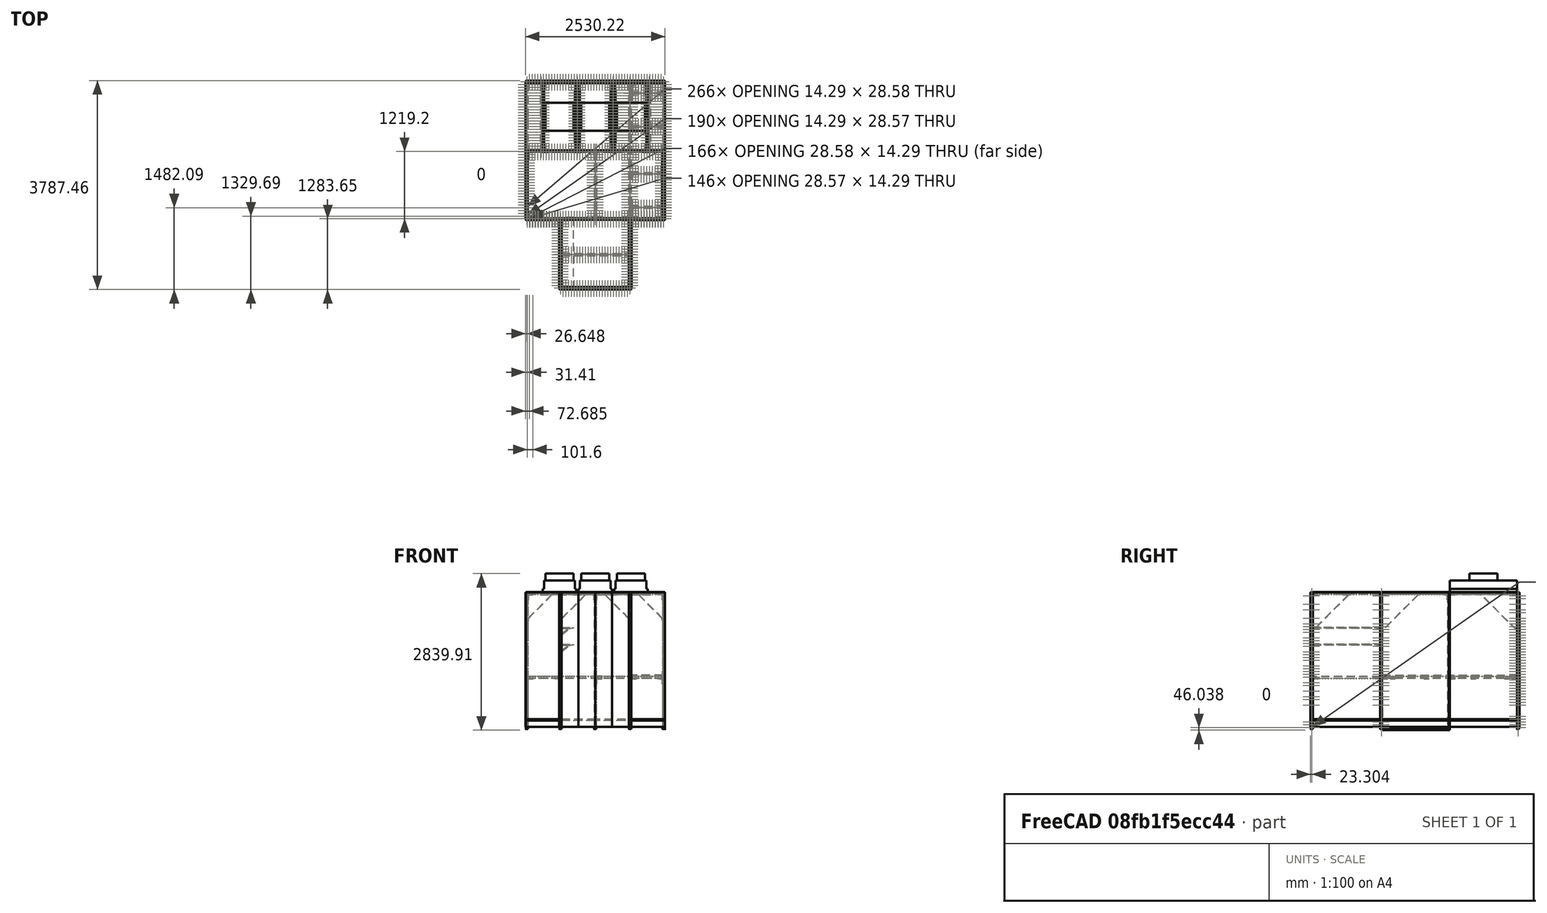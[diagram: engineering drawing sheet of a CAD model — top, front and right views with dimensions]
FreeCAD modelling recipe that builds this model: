
FCSTD DOCUMENT  (FreeCAD 0.18R16146 (Git))
Label: Clean Room
License: All rights reserved
LicenseURL: http://en.wikipedia.org/wiki/All_rights_reserved
objects: Part::Feature×99, Sketcher::SketchObject×67, PartDesign::Pad×57, PartDesign::Body×45, PartDesign::Fillet×12, PartDesign::Pocket×10, Mesh::Feature×3
note: 357 computed .brp shape members not serialized (recipe doc carries the construction recipe); baked Part::Feature solids carry a one-line shape summary decoded from their .brp

FEATURE [Part::Feature] Part__Feature  label="8ft_Strut_Channel_3310T184_001"
  Placement = pos=(-20.6375,5.55e-13,2459.29) rot=(-0.57735,-0.57735,0.57735;4.18879rad)
  shape: bbox 41.28 x 2438 x 41.28 mm, 272 faces (baked)
FEATURE [Part::Feature] Part__Feature001  label="8ft_Strut_Channel_3310T184_002"
  Placement = pos=(-2479.68,-20.6375,2459.29) rot=(-0.707107,0,0.707107;3.14159rad)
  shape: bbox 2438 x 41.28 x 41.28 mm, 272 faces (baked)
FEATURE [Part::Feature] Part__Feature002  label="8ft_Strut_Channel_3310T184_003"
  Placement = pos=(-2479.68,2459.04,2459.29) rot=(-0.707107,0,0.707107;3.14159rad)
  shape: bbox 2438 x 41.28 x 41.28 mm, 272 faces (baked)
FEATURE [Part::Feature] Part__Feature003  label="8ft_Strut_Channel_3310T184_004"
  Placement = pos=(-2500.31,5.6e-13,2459.29) rot=(-0.57735,-0.57735,0.57735;4.18879rad)
  shape: bbox 41.28 x 2438 x 41.28 mm, 272 faces (baked)
FEATURE [Part::Feature] Part__Feature004  label="8ft_Strut_Channel_3310T184_005"
  Placement = pos=(-20.6375,3e-15,20.6375) rot=(0.707107,0.707107,0;3.14159rad)
  shape: bbox 41.28 x 41.28 x 2438 mm, 272 faces (baked)
FEATURE [Part::Feature] Part__Feature005  label="8ft_Strut_Channel_3310T184_006"
  Placement = pos=(-2500.31,1.4e-14,20.6375) rot=(0.707107,0.707107,0;3.14159rad)
  shape: bbox 41.28 x 41.28 x 2438 mm, 272 faces (baked)
FEATURE [Part::Feature] Part__Feature006  label="8ft_Strut_Channel_3310T184_007"
  Placement = pos=(-2479.68,2459.04,20.6375) rot=(1,0,0;3.14159rad)
  shape: bbox 41.28 x 41.28 x 2438 mm, 272 faces (baked)
FEATURE [Part::Feature] Part__Feature007  label="8ft_Strut_Channel_3310T184_008"
  Placement = pos=(-41.021,2459.04,20.6375) rot=(0,-1,0;3.14159rad)
  shape: bbox 41.28 x 41.28 x 2438 mm, 272 faces (baked)
FEATURE [Part::Feature] Part__Feature008  label="8ft_Strut_Channel_3310T184_009"
  Placement = pos=(-650.621,-20.6375,20.6375) rot=(0,-1,0;3.14159rad)
  shape: bbox 41.28 x 41.28 x 2438 mm, 272 faces (baked)
FEATURE [Part::Feature] Part__Feature009  label="8ft_Strut_Channel_3310T184_010"
  Placement = pos=(-1911.1,-20.6375,20.6375) rot=(0,1,0;3.14159rad)
  shape: bbox 41.28 x 41.28 x 2438 mm, 272 faces (baked)
FEATURE [Part::Feature] Part__Feature010  label="8ft_Strut_Channel_3310T184_011"
  Placement = pos=(-1911.22,-1280.99,20.6375) rot=(0,1,0;3.14159rad)
  shape: bbox 41.28 x 41.28 x 2438 mm, 272 faces (baked)
FEATURE [Part::Feature] Part__Feature011  label="8ft_Strut_Channel_3310T184_012"
  Placement = pos=(-609.727,-1280.99,20.6375) rot=(1,0,0;3.14159rad)
  shape: bbox 41.28 x 41.28 x 2438 mm, 272 faces (baked)
FEATURE [Part::Feature] Part__Feature012  label="4ft_Strut_Channel_3310T181_001"
  Placement = pos=(-630.238,-1260.47,2459.29) rot=(-0.57735,-0.57735,0.57735;4.18879rad)
  shape: bbox 41.28 x 1219 x 41.28 mm, 152 faces (baked)
FEATURE [Part::Feature] Part__Feature013  label="4ft_Strut_Channel_3310T181_002"
  Placement = pos=(-650.875,-1281.11,2459.29) rot=(0,-1,0;4.71239rad)
  shape: bbox 1219 x 41.28 x 41.28 mm, 152 faces (baked)
FEATURE [Part::Feature] Part__Feature014  label="4ft_Strut_Channel_3310T181_003"
  Placement = pos=(-1890.71,-1260.47,2459.29) rot=(-0.57735,-0.57735,0.57735;4.18879rad)
  shape: bbox 41.28 x 1219 x 41.28 mm, 152 faces (baked)
FEATURE [Part::Feature] Part__Feature015  label="Double_90Deg_Bracket_33125T481_001"
  Placement = pos=(-20.6375,-20.6375,2459.04) rot=(-1,0,0;1.5708rad)
  shape: bbox 136.5 x 136.5 x 98.43 mm, 37 faces (baked)
FEATURE [Part::Feature] Part__Feature016  label="Double_90Deg_Bracket_33125T481_002"
  Placement = pos=(-2500.31,-20.6375,2459.04) rot=(0.57735,-0.57735,0.57735;4.18879rad)
  shape: bbox 136.5 x 136.5 x 98.43 mm, 37 faces (baked)
FEATURE [Part::Feature] Part__Feature017  label="Double_90Deg_Bracket_33125T481_003"
  Placement = pos=(-2500.31,2459.04,2459.04) rot=(0,0.707107,-0.707107;3.14159rad)
  shape: bbox 136.5 x 136.5 x 98.43 mm, 37 faces (baked)
FEATURE [Part::Feature] Part__Feature018  label="Double_90Deg_Bracket_33125T481_004"
  Placement = pos=(-20.6375,2459.04,2459.04) rot=(0.57735,0.57735,-0.57735;4.18879rad)
  shape: bbox 136.5 x 136.5 x 98.43 mm, 37 faces (baked)
FEATURE [Part::Feature] Part__Feature019  label="Double_90Deg_Bracket_33125T481_005"
  Placement = pos=(-1890.71,-1281.11,2459.04) rot=(0.57735,-0.57735,0.57735;4.18879rad)
  shape: bbox 136.5 x 136.5 x 98.43 mm, 37 faces (baked)
FEATURE [Part::Feature] Part__Feature020  label="Double_90Deg_Bracket_33125T481_006"
  Placement = pos=(-630.238,-1281.11,2459.04) rot=(-1,0,0;1.5708rad)
  shape: bbox 136.5 x 136.5 x 98.43 mm, 37 faces (baked)
FEATURE [Part::Feature] Part__Feature021  label="Triple_90Deg_Bracket_33125T484_001"
  Placement = pos=(-630.238,-20.6375,2459.04) rot=(0,0.707107,-0.707107;3.14159rad)
  shape: bbox 231.8 x 136.5 x 98.43 mm, 57 faces, 2 solids (baked)
FEATURE [Part::Feature] Part__Feature022  label="Triple_90Deg_Bracket_33125T484_002"
  Placement = pos=(-1890.71,-20.6375,2459.04) rot=(0,0.707107,-0.707107;3.14159rad)
  shape: bbox 231.8 x 136.5 x 98.43 mm, 57 faces, 2 solids (baked)
FEATURE [Part::Feature] Part__Feature023  label="8ft_Strut_Channel_3310T184_013"
  Placement = pos=(-2479.68,2459.04,976.312) rot=(0,-1,0;1.5708rad)
  shape: bbox 2438 x 41.28 x 41.28 mm, 272 faces (baked)
FEATURE [Part::Feature] Part__Feature024  label="8ft_Strut_Channel_3310T184_014"
  Placement = pos=(-2500.31,8.85e-13,976.312) rot=(0.57735,-0.57735,0.57735;2.0944rad)
  shape: bbox 41.28 x 2438 x 41.28 mm, 272 faces (baked)
FEATURE [Part::Feature] Part__Feature025  label="8ft_Strut_Channel_3310T184_015"
  Placement = pos=(-20.6375,2.17e-13,976.312) rot=(0.57735,-0.57735,0.57735;2.0944rad)
  shape: bbox 41.28 x 2438 x 41.28 mm, 272 faces (baked)
FEATURE [Part::Feature] Part__Feature026  label="8ft_Strut_Channel_3310T184_016"
  Placement = pos=(-630.238,2.18e-13,976.312) rot=(0.57735,-0.57735,0.57735;2.0944rad)
  shape: bbox 41.28 x 2438 x 41.28 mm, 272 faces (baked)
FEATURE [Part::Feature] Part__Feature027  label="Double_90Deg_Bracket_33125T481_007"
  Placement = pos=(-20.6375,2459.04,935.037) rot=(0.57735,0.57735,-0.57735;4.18879rad)
  shape: bbox 136.5 x 136.5 x 98.43 mm, 37 faces (baked)
FEATURE [Part::Feature] Part__Feature028  label="Double_90Deg_Bracket_33125T481_008"
  Placement = pos=(-2500.31,2459.04,935.037) rot=(0,0.707107,-0.707107;3.14159rad)
  shape: bbox 136.5 x 136.5 x 98.43 mm, 37 faces (baked)
FEATURE [Part::Feature] Part__Feature029  label="4ft_Strut_Channel_3310T181_004"
  Placement = pos=(-1890.71,-1260.47,935.291) rot=(0.57735,0.57735,-0.57735;2.0944rad)
  shape: bbox 41.28 x 1219 x 41.28 mm, 152 faces (baked)
FEATURE [Part::Feature] Part__Feature030  label="4ft_Strut_Channel_3310T181_005"
  Placement = pos=(-630.237,-1260.47,935.291) rot=(0.57735,0.57735,-0.57735;2.0944rad)
  shape: bbox 41.28 x 1219 x 41.28 mm, 152 faces (baked)
FEATURE [Part::Feature] Part__Feature031  label="2ft_Strut_Channel_3310T475_001"
  Placement = pos=(-609.6,-20.6375,976.312) rot=(0,-1,0;1.5708rad)
  shape: bbox 609.6 x 41.28 x 41.28 mm, 92 faces (baked)
FEATURE [Part::Feature] Part__Feature032  label="2ft_Strut_Channel_3310T475_002"
  Placement = pos=(-2520.95,-20.6375,976.312) rot=(0,-1,0;1.5708rad)
  shape: bbox 609.6 x 41.28 x 41.28 mm, 92 faces (baked)
FEATURE [Part::Feature] Part__Feature033  label="Double_90Deg_Bracket_33125T481_009"
  Placement = pos=(-20.6375,-20.6375,935.037) rot=(-1,0,0;1.5708rad)
  shape: bbox 136.5 x 136.5 x 98.43 mm, 37 faces (baked)
FEATURE [Part::Feature] Part__Feature034  label="Double_90Deg_Bracket_33125T481_010"
  Placement = pos=(-2500.31,-20.6375,935.037) rot=(0.57735,-0.57735,0.57735;4.18879rad)
  shape: bbox 136.5 x 136.5 x 98.43 mm, 37 faces (baked)
FEATURE [Part::Feature] Part__Feature035  label="Triple_90Deg_Bracket_33125T484_003"
  Placement = pos=(-630.238,-20.6375,935.037) rot=(0.57735,-0.57735,0.57735;4.18879rad)
  shape: bbox 136.5 x 231.8 x 98.43 mm, 57 faces, 2 solids (baked)
FEATURE [Part::Feature] Part__Feature036  label="Double_90Deg_Bracket_33125T481_011"
  Placement = pos=(-1890.71,-20.6375,935.037) rot=(0.57735,0.57735,-0.57735;4.18879rad)
  shape: bbox 136.5 x 136.5 x 98.43 mm, 37 faces (baked)
FEATURE [Part::Feature] Part__Feature037  label="90Deg_Bracket_33125T34_001"
  Placement = pos=(-630.238,-1260.48,935.037) rot=(0,1,0;1.5708rad)
  shape: bbox 41.28 x 104.8 x 88.9 mm, 18 faces (baked)
FEATURE [Part::Feature] Part__Feature038  label="90Deg_Bracket_33125T34_002"
  Placement = pos=(-1890.71,-1260.48,935.037) rot=(0,1,0;1.5708rad)
  shape: bbox 41.28 x 104.8 x 88.9 mm, 18 faces (baked)
FEATURE [Part::Feature] Part__Feature043  label="36in_Brace_3574T51_001"
  Placement = pos=(-20.5105,2115.06,2135.57) rot=(0.707107,0,0.707107;3.14159rad)
  shape: bbox 41.28 x 687.9 x 687.9 mm, 14 faces (baked)
FEATURE [Part::Feature] Part__Feature044  label="36in_Brace_3574T51_002"
  Placement = pos=(-2499.93,2115.06,2135.57) rot=(0.707107,0,0.707107;3.14159rad)
  shape: bbox 41.28 x 687.9 x 687.9 mm, 14 faces (baked)
FEATURE [Part::Feature] Part__Feature045  label="36in_Brace_3574T51_003"
  Placement = pos=(-2499.93,323.338,2135.57) rot=(-0.57735,0.57735,-0.57735;2.0944rad)
  shape: bbox 41.28 x 687.9 x 687.9 mm, 14 faces (baked)
FEATURE [Part::Feature] Part__Feature046  label="36in_Brace_3574T51_004"
  Placement = pos=(-20.5105,323.338,2135.57) rot=(-0.57735,0.57735,-0.57735;2.0944rad)
  shape: bbox 41.28 x 687.9 x 687.9 mm, 14 faces (baked)
FEATURE [Part::Feature] Part__Feature047  label="2ft_Strut_Channel_3310T475_003"
  Placement = pos=(-609.6,792.163,976.312) rot=(0,-1,0;1.5708rad)
  shape: bbox 609.6 x 41.28 x 41.28 mm, 92 faces (baked)
FEATURE [Part::Feature] Part__Feature048  label="2ft_Strut_Channel_3310T475_004"
  Placement = pos=(-609.6,1645.98,976.312) rot=(0,-1,0;1.5708rad)
  shape: bbox 609.6 x 41.28 x 41.28 mm, 92 faces (baked)
FEATURE [Part::Feature] Part__Feature049  label="Small_Tee_Bracket_33125T466_001"
  Placement = pos=(-92.2973,792.289,931.866) rot=(0,0,1;1.5708rad)
  shape: bbox 88.9 x 88.9 x 6.35 mm, 14 faces (baked)
FEATURE [Part::Feature] Part__Feature050  label="Small_Tee_Bracket_33125T466_002"
  Placement = pos=(-92.2972,1646.11,931.866) rot=(0,0,1;1.5708rad)
  shape: bbox 88.9 x 88.9 x 6.35 mm, 14 faces (baked)
FEATURE [Part::Feature] Part__Feature051  label="Small_Tee_Bracket_33125T466_003"
  Placement = pos=(-558.324,1646.11,931.866) rot=(0,0,-1;1.5708rad)
  shape: bbox 88.9 x 88.9 x 6.35 mm, 14 faces (baked)
FEATURE [Part::Feature] Part__Feature052  label="Small_Tee_Bracket_33125T466_004"
  Placement = pos=(-558.324,792.29,931.866) rot=(0,0,-1;1.5708rad)
  shape: bbox 88.9 x 88.9 x 6.35 mm, 14 faces (baked)
FEATURE [Part::Feature] Part__Feature053  label="5ft_Strut_Channel_3310T39_001"
  Placement = pos=(-20.5105,1219.2,934.91) rot=(0.707107,0.707107,0;3.14159rad)
  shape: bbox 41.28 x 41.28 x 1524 mm, 182 faces (baked)
FEATURE [Part::Feature] Part__Feature054  label="5ft_Strut_Channel_3310T39_002"
  Placement = pos=(-2499.93,1219.2,934.91) rot=(0.707107,0.707107,0;3.14159rad)
  shape: bbox 41.28 x 41.28 x 1524 mm, 182 faces (baked)
FEATURE [Part::Feature] Part__Feature055  label="5ft_Strut_Channel_3310T39_003"
  Placement = pos=(-1239.71,2458.91,934.91) rot=(1,0,0;3.14159rad)
  shape: bbox 41.28 x 41.28 x 1524 mm, 182 faces (baked)
FEATURE [Part::Feature] Part__Feature056  label="3ft_Strut_Channel_3310T54_001"
  Placement = pos=(-20.5105,1219.2,20.5105) rot=(0.707107,0.707107,0;3.14159rad)
  shape: bbox 41.28 x 41.28 x 914.4 mm, 122 faces (baked)
FEATURE [Part::Feature] Part__Feature057  label="3ft_Strut_Channel_3310T54_002"
  Placement = pos=(-2499.93,1219.2,20.5105) rot=(0.707107,0.707107,0;3.14159rad)
  shape: bbox 41.28 x 41.28 x 914.4 mm, 122 faces (baked)
FEATURE [Part::Feature] Part__Feature058  label="3ft_Strut_Channel_3310T54_003"
  Placement = pos=(-1239.71,2458.91,20.5105) rot=(1,0,0;3.14159rad)
  shape: bbox 41.28 x 41.28 x 914.4 mm, 122 faces (baked)
FEATURE [Part::Feature] Part__Feature059  label="Wraparound_Wing_Bracket_33125T491_001"
  Placement = pos=(-20.5105,1219.41,955.982) rot=(0,-1,0;1.5708rad)
  shape: bbox 47.63 x 98.43 x 232.6 mm, 44 faces (baked)
FEATURE [Part::Feature] Part__Feature061  label="Wraparound_Wing_Bracket_33125T491_002"
  Placement = pos=(-2499.93,1219.41,955.982) rot=(0,1,0;1.5708rad)
  shape: bbox 47.63 x 98.43 x 232.6 mm, 44 faces (baked)
FEATURE [Part::Feature] Part__Feature063  label="Wraparound_Wing_Bracket_33125T491_003"
  Placement = pos=(-1260.22,2459.12,2458.38) rot=(0,0.707107,-0.707107;3.14159rad)
  shape: bbox 232.6 x 47.63 x 98.43 mm, 44 faces (baked)
FEATURE [Part::Feature] Part__Feature064  label="Wraparound_Wing_Bracket_33125T491_004"
  Placement = pos=(-1239.71,2459.12,955.982) rot=(0.57735,0.57735,-0.57735;2.0944rad)
  shape: bbox 98.43 x 47.63 x 232.6 mm, 44 faces (baked)
FEATURE [Part::Feature] Part__Feature065  label="24in_Corner_Brace_3574T41_001"
  Placement = pos=(-866.569,-20.5105,2242.69) rot=(-1,0,0;1.5708rad)
  shape: bbox 472.3 x 41.28 x 472.3 mm, 14 faces (baked)
FEATURE [Part::Feature] Part__Feature066  label="24in_Corner_Brace_3574T41_002"
  Placement = pos=(-866.569,-1280.73,2242.69) rot=(-1,0,0;1.5708rad)
  shape: bbox 472.3 x 41.28 x 472.3 mm, 14 faces (baked)
FEATURE [Part::Feature] Part__Feature067  label="24in_Corner_Brace_3574T41_003"
  Placement = pos=(-1654.65,-20.5105,2242.69) rot=(0,0.707107,-0.707107;3.14159rad)
  shape: bbox 472.3 x 41.28 x 472.3 mm, 14 faces (baked)
FEATURE [Part::Feature] Part__Feature068  label="24in_Corner_Brace_3574T41_004"
  Placement = pos=(-1654.65,-1280.73,2242.69) rot=(0,0.707107,-0.707107;3.14159rad)
  shape: bbox 472.3 x 41.28 x 472.3 mm, 14 faces (baked)
FEATURE [Part::Feature] Part__Feature069  label="36in_Brace_3574T51_005"
  Placement = pos=(-630.111,-936.883,2135.57) rot=(-0.57735,0.57735,-0.57735;2.0944rad)
  shape: bbox 41.28 x 687.9 x 687.9 mm, 14 faces (baked)
FEATURE [Part::Feature] Part__Feature070  label="36in_Brace_3574T51_006"
  Placement = pos=(-1890.33,-936.883,2135.57) rot=(-0.57735,0.57735,-0.57735;2.0944rad)
  shape: bbox 41.28 x 687.9 x 687.9 mm, 14 faces (baked)
FEATURE [Part::Feature] Part__Feature071  label="24in_Corner_Brace_3574T41_005"
  Placement = pos=(-256.969,2458.91,2242.69) rot=(-1,0,0;1.5708rad)
  shape: bbox 472.3 x 41.28 x 472.3 mm, 14 faces (baked)
FEATURE [Part::Feature] Part__Feature072  label="24in_Corner_Brace_3574T41_006"
  Placement = pos=(-2264.25,2458.91,2242.69) rot=(0,0.707107,-0.707107;3.14159rad)
  shape: bbox 472.3 x 41.28 x 472.3 mm, 14 faces (baked)
FEATURE [Sketcher::SketchObject] Sketch
  MapMode = 5
  Support = -> [XY_Plane]
  sketch-geometry (4):
    g0: LineSegment StartX=0 StartY=0 StartZ=0 EndX=1219.2 EndY=0 EndZ=0
    g1: LineSegment StartX=1219.2 StartY=0 StartZ=0 EndX=1219.2 EndY=609.6 EndZ=0
    g2: LineSegment StartX=1219.2 StartY=609.6 StartZ=0 EndX=0 EndY=609.6 EndZ=0
    g3: LineSegment StartX=0 StartY=609.6 StartZ=0 EndX=0 EndY=0 EndZ=0
  constraints (11):
    c: Coincident(g0,g1)
    c: Coincident(g1,g2)
    c: Coincident(g2,g3)
    c: Coincident(g3,g0)
    c: Horizontal(g0)
    c: Horizontal(g2)
    c: Vertical(g1)
    c: Vertical(g3)
    c: Coincident(g0,g-1)
    c: DistanceX(g2,g2) = 1219.2
    c: DistanceY(g1,g1) = 609.6
FEATURE [PartDesign::Pad] Pad
  Length = 101.6
  Length2 = 100
  Profile = -> Sketch
  Type = 0
FEATURE [Sketcher::SketchObject] Sketch001
  ExternalGeometry = -> [Pad]
  MapMode = 5
  Placement = pos=(0,0,101.6) rot=(0,0,1;0rad)
  Support = -> [Pad]
  sketch-geometry (6):
    g0: LineSegment StartX=1219.2 StartY=584.2 StartZ=0 EndX=0 EndY=584.2 EndZ=0
    g1: LineSegment StartX=0 StartY=584.2 StartZ=0 EndX=0 EndY=25.4 EndZ=0
    g2: LineSegment StartX=0 StartY=25.4 StartZ=0 EndX=1219.2 EndY=25.4 EndZ=0
    g3: LineSegment StartX=1219.2 StartY=25.4 StartZ=0 EndX=1219.2 EndY=584.2 EndZ=0
    g4: LineSegment [constr] StartX=1219.2 StartY=609.6 StartZ=0 EndX=1219.2 EndY=584.2 EndZ=0
    g5: LineSegment [constr] StartX=1219.2 StartY=25.4 StartZ=0 EndX=1219.2 EndY=0 EndZ=0
  constraints (16):
    c: Coincident(g0,g1)
    c: Coincident(g1,g2)
    c: Coincident(g2,g3)
    c: Coincident(g3,g0)
    c: Horizontal(g0)
    c: Horizontal(g2)
    c: Vertical(g1)
    c: Vertical(g3)
    c: PointOnObject(g0,g-3)
    c: PointOnObject(g1,g-2)
    c: Coincident(g4,g-3)
    c: Coincident(g4,g0)
    c: Coincident(g5,g2)
    c: Coincident(g5,g-3)
    c: Equal(g5,g4)
    c: DistanceY(g4,g4) = 25.4
FEATURE [PartDesign::Pad] Pad001
  BaseFeature = -> Pad
  Length = 152.4
  Length2 = 100
  Profile = -> Sketch001
  Type = 0
FEATURE [Sketcher::SketchObject] Sketch002
  ExternalGeometry = -> [Pad001]
  MapMode = 5
  Placement = pos=(0,0,254) rot=(0,0,1;0rad)
  Support = -> [Pad001]
  sketch-geometry (8):
    g0: LineSegment StartX=355.6 StartY=558.8 StartZ=0 EndX=863.6 EndY=558.8 EndZ=0
    g1: LineSegment StartX=863.6 StartY=558.8 StartZ=0 EndX=863.6 EndY=50.8 EndZ=0
    g2: LineSegment StartX=863.6 StartY=50.8 StartZ=0 EndX=355.6 EndY=50.8 EndZ=0
    g3: LineSegment StartX=355.6 StartY=50.8 StartZ=0 EndX=355.6 EndY=558.8 EndZ=0
    g4: LineSegment [constr] StartX=863.6 StartY=558.8 StartZ=0 EndX=863.6 EndY=584.2 EndZ=0
    g5: LineSegment [constr] StartX=863.6 StartY=50.8 StartZ=0 EndX=863.6 EndY=25.4 EndZ=0
    g6: LineSegment [constr] StartX=355.6 StartY=558.8 StartZ=0 EndX=0 EndY=558.8 EndZ=0
    g7: LineSegment [constr] StartX=863.6 StartY=558.8 StartZ=0 EndX=1219.2 EndY=558.8 EndZ=0
  constraints (24):
    c: Coincident(g0,g1)
    c: Coincident(g1,g2)
    c: Coincident(g2,g3)
    c: Coincident(g3,g0)
    c: Horizontal(g0)
    c: Horizontal(g2)
    c: Vertical(g1)
    c: Vertical(g3)
    c: Coincident(g4,g0)
    c: PointOnObject(g4,g-4)
    c: Vertical(g4)
    c: Coincident(g5,g1)
    c: PointOnObject(g5,g-5)
    c: Vertical(g5)
    c: Coincident(g6,g0)
    c: PointOnObject(g6,g-2)
    c: Horizontal(g6)
    c: Coincident(g7,g0)
    c: PointOnObject(g7,g-3)
    c: Horizontal(g7)
    c: Equal(g7,g6)
    c: Equal(g4,g5)
    c: DistanceY(g4,g4) = 25.4
    c: Equal(g0,g3)
FEATURE [PartDesign::Pad] Pad002
  BaseFeature = -> Pad001
  Length = 127
  Length2 = 100
  Profile = -> Sketch002
  Type = 0
FEATURE [PartDesign::Body] Body  label="Fan_Filter_Unit_001"
  Group = -> [Sketch,Pad,Sketch001,Pad001,Sketch002,Pad002]
  Origin = -> Origin
  Placement = pos=(-307.657,1219.2,2458.91) rot=(0,0,1;1.5708rad)
  Tip = -> Pad002
FEATURE [Sketcher::SketchObject] Sketch003
  MapMode = 5
  Support = -> [XY_Plane001]
  sketch-geometry (4):
    g0: LineSegment StartX=0 StartY=0 StartZ=0 EndX=1219.2 EndY=0 EndZ=0
    g1: LineSegment StartX=1219.2 StartY=0 StartZ=0 EndX=1219.2 EndY=609.6 EndZ=0
    g2: LineSegment StartX=1219.2 StartY=609.6 StartZ=0 EndX=0 EndY=609.6 EndZ=0
    g3: LineSegment StartX=0 StartY=609.6 StartZ=0 EndX=0 EndY=0 EndZ=0
  constraints (11):
    c: Coincident(g0,g1)
    c: Coincident(g1,g2)
    c: Coincident(g2,g3)
    c: Coincident(g3,g0)
    c: Horizontal(g0)
    c: Horizontal(g2)
    c: Vertical(g1)
    c: Vertical(g3)
    c: Coincident(g0,g-1)
    c: DistanceX(g2,g2) = 1219.2
    c: DistanceY(g1,g1) = 609.6
FEATURE [PartDesign::Pad] Pad004
  Length = 101.6
  Length2 = 100
  Profile = -> Sketch003
  Type = 0
FEATURE [Sketcher::SketchObject] Sketch005
  ExternalGeometry = -> [Pad004]
  MapMode = 5
  Placement = pos=(0,0,101.6) rot=(0,0,1;0rad)
  Support = -> [Pad004]
  sketch-geometry (6):
    g0: LineSegment StartX=1219.2 StartY=584.2 StartZ=0 EndX=0 EndY=584.2 EndZ=0
    g1: LineSegment StartX=0 StartY=584.2 StartZ=0 EndX=0 EndY=25.4 EndZ=0
    g2: LineSegment StartX=0 StartY=25.4 StartZ=0 EndX=1219.2 EndY=25.4 EndZ=0
    g3: LineSegment StartX=1219.2 StartY=25.4 StartZ=0 EndX=1219.2 EndY=584.2 EndZ=0
    g4: LineSegment [constr] StartX=1219.2 StartY=609.6 StartZ=0 EndX=1219.2 EndY=584.2 EndZ=0
    g5: LineSegment [constr] StartX=1219.2 StartY=25.4 StartZ=0 EndX=1219.2 EndY=0 EndZ=0
  constraints (16):
    c: Coincident(g0,g1)
    c: Coincident(g1,g2)
    c: Coincident(g2,g3)
    c: Coincident(g3,g0)
    c: Horizontal(g0)
    c: Horizontal(g2)
    c: Vertical(g1)
    c: Vertical(g3)
    c: PointOnObject(g0,g-3)
    c: PointOnObject(g1,g-2)
    c: Coincident(g4,g-3)
    c: Coincident(g4,g0)
    c: Coincident(g5,g2)
    c: Coincident(g5,g-3)
    c: Equal(g5,g4)
    c: DistanceY(g4,g4) = 25.4
FEATURE [PartDesign::Pad] Pad005
  BaseFeature = -> Pad004
  Length = 152.4
  Length2 = 100
  Profile = -> Sketch005
  Type = 0
FEATURE [Sketcher::SketchObject] Sketch004
  ExternalGeometry = -> [Pad005]
  MapMode = 5
  Placement = pos=(0,0,254) rot=(0,0,1;0rad)
  Support = -> [Pad005]
  sketch-geometry (8):
    g0: LineSegment StartX=355.6 StartY=558.8 StartZ=0 EndX=863.6 EndY=558.8 EndZ=0
    g1: LineSegment StartX=863.6 StartY=558.8 StartZ=0 EndX=863.6 EndY=50.8 EndZ=0
    g2: LineSegment StartX=863.6 StartY=50.8 StartZ=0 EndX=355.6 EndY=50.8 EndZ=0
    g3: LineSegment StartX=355.6 StartY=50.8 StartZ=0 EndX=355.6 EndY=558.8 EndZ=0
    g4: LineSegment [constr] StartX=863.6 StartY=558.8 StartZ=0 EndX=863.6 EndY=584.2 EndZ=0
    g5: LineSegment [constr] StartX=863.6 StartY=50.8 StartZ=0 EndX=863.6 EndY=25.4 EndZ=0
    g6: LineSegment [constr] StartX=355.6 StartY=558.8 StartZ=0 EndX=0 EndY=558.8 EndZ=0
    g7: LineSegment [constr] StartX=863.6 StartY=558.8 StartZ=0 EndX=1219.2 EndY=558.8 EndZ=0
  constraints (24):
    c: Coincident(g0,g1)
    c: Coincident(g1,g2)
    c: Coincident(g2,g3)
    c: Coincident(g3,g0)
    c: Horizontal(g0)
    c: Horizontal(g2)
    c: Vertical(g1)
    c: Vertical(g3)
    c: Coincident(g4,g0)
    c: PointOnObject(g4,g-4)
    c: Vertical(g4)
    c: Coincident(g5,g1)
    c: PointOnObject(g5,g-5)
    c: Vertical(g5)
    c: Coincident(g6,g0)
    c: PointOnObject(g6,g-2)
    c: Horizontal(g6)
    c: Coincident(g7,g0)
    c: PointOnObject(g7,g-3)
    c: Horizontal(g7)
    c: Equal(g7,g6)
    c: Equal(g4,g5)
    c: DistanceY(g4,g4) = 25.4
    c: Equal(g0,g3)
FEATURE [PartDesign::Pad] Pad003
  BaseFeature = -> Pad005
  Length = 127
  Length2 = 100
  Profile = -> Sketch004
  Type = 0
FEATURE [PartDesign::Body] Body001  label="Fan_Filter_Unit_002"
  Group = -> [Sketch003,Pad004,Sketch005,Pad005,Sketch004,Pad003]
  Origin = -> Origin001
  Placement = pos=(-1603.18,1219.2,2458.91) rot=(0,0,1;1.5708rad)
  Tip = -> Pad003
FEATURE [Sketcher::SketchObject] Sketch008
  MapMode = 5
  Support = -> [XY_Plane002]
  sketch-geometry (4):
    g0: LineSegment StartX=0 StartY=0 StartZ=0 EndX=1219.2 EndY=0 EndZ=0
    g1: LineSegment StartX=1219.2 StartY=0 StartZ=0 EndX=1219.2 EndY=609.6 EndZ=0
    g2: LineSegment StartX=1219.2 StartY=609.6 StartZ=0 EndX=0 EndY=609.6 EndZ=0
    g3: LineSegment StartX=0 StartY=609.6 StartZ=0 EndX=0 EndY=0 EndZ=0
  constraints (11):
    c: Coincident(g0,g1)
    c: Coincident(g1,g2)
    c: Coincident(g2,g3)
    c: Coincident(g3,g0)
    c: Horizontal(g0)
    c: Horizontal(g2)
    c: Vertical(g1)
    c: Vertical(g3)
    c: Coincident(g0,g-1)
    c: DistanceX(g2,g2) = 1219.2
    c: DistanceY(g1,g1) = 609.6
FEATURE [PartDesign::Pad] Pad008
  Length = 101.6
  Length2 = 100
  Profile = -> Sketch008
  Type = 0
FEATURE [Sketcher::SketchObject] Sketch007
  ExternalGeometry = -> [Pad008]
  MapMode = 5
  Placement = pos=(0,0,101.6) rot=(0,0,1;0rad)
  Support = -> [Pad008]
  sketch-geometry (6):
    g0: LineSegment StartX=1219.2 StartY=584.2 StartZ=0 EndX=0 EndY=584.2 EndZ=0
    g1: LineSegment StartX=0 StartY=584.2 StartZ=0 EndX=0 EndY=25.4 EndZ=0
    g2: LineSegment StartX=0 StartY=25.4 StartZ=0 EndX=1219.2 EndY=25.4 EndZ=0
    g3: LineSegment StartX=1219.2 StartY=25.4 StartZ=0 EndX=1219.2 EndY=584.2 EndZ=0
    g4: LineSegment [constr] StartX=1219.2 StartY=609.6 StartZ=0 EndX=1219.2 EndY=584.2 EndZ=0
    g5: LineSegment [constr] StartX=1219.2 StartY=25.4 StartZ=0 EndX=1219.2 EndY=0 EndZ=0
  constraints (16):
    c: Coincident(g0,g1)
    c: Coincident(g1,g2)
    c: Coincident(g2,g3)
    c: Coincident(g3,g0)
    c: Horizontal(g0)
    c: Horizontal(g2)
    c: Vertical(g1)
    c: Vertical(g3)
    c: PointOnObject(g0,g-3)
    c: PointOnObject(g1,g-2)
    c: Coincident(g4,g-3)
    c: Coincident(g4,g0)
    c: Coincident(g5,g2)
    c: Coincident(g5,g-3)
    c: Equal(g5,g4)
    c: DistanceY(g4,g4) = 25.4
FEATURE [PartDesign::Pad] Pad006
  BaseFeature = -> Pad008
  Length = 152.4
  Length2 = 100
  Profile = -> Sketch007
  Type = 0
FEATURE [Sketcher::SketchObject] Sketch006
  ExternalGeometry = -> [Pad006]
  MapMode = 5
  Placement = pos=(0,0,254) rot=(0,0,1;0rad)
  Support = -> [Pad006]
  sketch-geometry (8):
    g0: LineSegment StartX=355.6 StartY=558.8 StartZ=0 EndX=863.6 EndY=558.8 EndZ=0
    g1: LineSegment StartX=863.6 StartY=558.8 StartZ=0 EndX=863.6 EndY=50.8 EndZ=0
    g2: LineSegment StartX=863.6 StartY=50.8 StartZ=0 EndX=355.6 EndY=50.8 EndZ=0
    g3: LineSegment StartX=355.6 StartY=50.8 StartZ=0 EndX=355.6 EndY=558.8 EndZ=0
    g4: LineSegment [constr] StartX=863.6 StartY=558.8 StartZ=0 EndX=863.6 EndY=584.2 EndZ=0
    g5: LineSegment [constr] StartX=863.6 StartY=50.8 StartZ=0 EndX=863.6 EndY=25.4 EndZ=0
    g6: LineSegment [constr] StartX=355.6 StartY=558.8 StartZ=0 EndX=0 EndY=558.8 EndZ=0
    g7: LineSegment [constr] StartX=863.6 StartY=558.8 StartZ=0 EndX=1219.2 EndY=558.8 EndZ=0
  constraints (24):
    c: Coincident(g0,g1)
    c: Coincident(g1,g2)
    c: Coincident(g2,g3)
    c: Coincident(g3,g0)
    c: Horizontal(g0)
    c: Horizontal(g2)
    c: Vertical(g1)
    c: Vertical(g3)
    c: Coincident(g4,g0)
    c: PointOnObject(g4,g-4)
    c: Vertical(g4)
    c: Coincident(g5,g1)
    c: PointOnObject(g5,g-5)
    c: Vertical(g5)
    c: Coincident(g6,g0)
    c: PointOnObject(g6,g-2)
    c: Horizontal(g6)
    c: Coincident(g7,g0)
    c: PointOnObject(g7,g-3)
    c: Horizontal(g7)
    c: Equal(g7,g6)
    c: Equal(g4,g5)
    c: DistanceY(g4,g4) = 25.4
    c: Equal(g0,g3)
FEATURE [PartDesign::Pad] Pad007
  BaseFeature = -> Pad006
  Length = 127
  Length2 = 100
  Profile = -> Sketch006
  Type = 0
FEATURE [PartDesign::Body] Body002  label="Fan_Filter_Unit_003"
  Group = -> [Sketch008,Pad008,Sketch007,Pad006,Sketch006,Pad007]
  Origin = -> Origin002
  Placement = pos=(-955.421,1219.2,2458.91) rot=(0,0,1;1.5708rad)
  Tip = -> Pad007
FEATURE [Part::Feature] Part__Feature073  label="8ft_Strut_Channel_3310T184_017"
  Placement = pos=(-2479.68,1198.56,2459.29) rot=(-0.707107,0,0.707107;3.14159rad)
  shape: bbox 2438 x 41.28 x 41.28 mm, 272 faces (baked)
FEATURE [Part::Feature] Part__Feature074  label="4ft_Strut_Channel_3310T181_006"
  Placement = pos=(-281.559,1218.95,2459.29) rot=(-0.57735,-0.57735,0.57735;4.18879rad)
  shape: bbox 41.28 x 1219 x 41.28 mm, 152 faces (baked)
FEATURE [Part::Feature] Part__Feature075  label="4ft_Strut_Channel_3310T181_007"
  Placement = pos=(-935.331,1218.95,2500.31) rot=(0.57735,-0.57735,0.57735;2.0944rad)
  shape: bbox 41.28 x 1219 x 41.28 mm, 152 faces (baked)
FEATURE [Part::Feature] Part__Feature076  label="4ft_Strut_Channel_3310T181_008"
  Placement = pos=(-1586.54,1218.95,2500.31) rot=(0.57735,-0.57735,0.57735;2.0944rad)
  shape: bbox 41.28 x 1219 x 41.28 mm, 152 faces (baked)
FEATURE [Part::Feature] Part__Feature077  label="4ft_Strut_Channel_3310T181_009"
  Placement = pos=(-2237.75,1218.95,2459.29) rot=(-0.57735,-0.57735,0.57735;4.18879rad)
  shape: bbox 41.28 x 1219 x 41.28 mm, 152 faces (baked)
FEATURE [Part::Feature] Part__Feature078  label="Triple_90Deg_Bracket_33125T484_004"
  Placement = pos=(-2500.9,1199.74,2459.04) rot=(0.57735,-0.57735,0.57735;4.18879rad)
  shape: bbox 136.5 x 231.8 x 98.43 mm, 57 faces, 2 solids (baked)
FEATURE [Part::Feature] Part__Feature079  label="Triple_90Deg_Bracket_33125T484_005"
  Placement = pos=(-21.4789,1199.74,2459.04) rot=(0.57735,0.57735,-0.57735;4.18879rad)
  shape: bbox 136.5 x 231.8 x 98.43 mm, 57 faces, 2 solids (baked)
FEATURE [Part::Feature] Part__Feature080  label="Large_Elbow_33125T22_001"
  Placement = pos=(-562.116,2390.97,932.587) rot=(0,0,-1;1.5708rad)
  shape: bbox 136.5 x 136.5 x 6.35 mm, 17 faces (baked)
FEATURE [Part::Feature] Part__Feature081  label="Large_Elbow_33125T22_002"
  Placement = pos=(-349.96,2390.97,2456.59) rot=(0,0,1;3.14159rad)
  shape: bbox 136.5 x 136.5 x 6.35 mm, 17 faces (baked)
FEATURE [Part::Feature] Part__Feature082  label="Large_Elbow_33125T22_003"
  Placement = pos=(-349.96,1266.63,2456.59) rot=(0,0,1;1.5708rad)
  shape: bbox 136.5 x 136.5 x 6.35 mm, 17 faces (baked)
FEATURE [Part::Feature] Part__Feature083  label="Large_Elbow_33125T22_004"
  Placement = pos=(-2169.63,1266.63,2456.59) rot=(0,0,1;0rad)
  shape: bbox 136.5 x 136.5 x 6.35 mm, 17 faces (baked)
FEATURE [Part::Feature] Part__Feature084  label="Large_Elbow_33125T22_005"
  Placement = pos=(-2169.63,2390.86,2456.59) rot=(0,0,-1;1.5708rad)
  shape: bbox 136.5 x 136.5 x 6.35 mm, 17 faces (baked)
FEATURE [Part::Feature] Part__Feature085  label="Large_Tee_Bracket_33125T77_001"
  Placement = pos=(-935.551,2343.22,2455.71) rot=(0,0,1;3.14159rad)
  shape: bbox 136.5 x 136.5 x 6.35 mm, 18 faces (baked)
FEATURE [Part::Feature] Part__Feature086  label="Large_Tee_Bracket_33125T77_002"
  Placement = pos=(-1586.76,2343.22,2455.71) rot=(0,0,1;3.14159rad)
  shape: bbox 136.5 x 136.5 x 6.35 mm, 18 faces (baked)
FEATURE [Part::Feature] Part__Feature087  label="Large_Tee_Bracket_33125T77_003"
  Placement = pos=(-1586.76,1314.49,2455.71) rot=(0,0,1;0rad)
  shape: bbox 136.5 x 136.5 x 6.35 mm, 18 faces (baked)
FEATURE [Part::Feature] Part__Feature088  label="Large_Tee_Bracket_33125T77_004"
  Placement = pos=(-935.551,1314.49,2455.71) rot=(0,0,1;0rad)
  shape: bbox 136.5 x 136.5 x 6.35 mm, 18 faces (baked)
FEATURE [Sketcher::SketchObject] Sketch009
  MapMode = 5
  Placement = pos=(0,0,0) rot=(0.57735,0.57735,0.57735;2.0944rad)
  Support = -> [YZ_Plane003]
  sketch-geometry (4):
    g0: LineSegment StartX=0 StartY=0 StartZ=0 EndX=1219.2 EndY=0 EndZ=0
    g1: LineSegment StartX=1219.2 StartY=0 StartZ=0 EndX=1219.2 EndY=2438.4 EndZ=0
    g2: LineSegment StartX=1219.2 StartY=2438.4 StartZ=0 EndX=0 EndY=2438.4 EndZ=0
    g3: LineSegment StartX=0 StartY=2438.4 StartZ=0 EndX=0 EndY=0 EndZ=0
  constraints (11):
    c: Coincident(g0,g1)
    c: Coincident(g1,g2)
    c: Coincident(g2,g3)
    c: Coincident(g3,g0)
    c: Horizontal(g0)
    c: Horizontal(g2)
    c: Vertical(g1)
    c: Vertical(g3)
    c: Coincident(g0,g-1)
    c: DistanceX(g0,g0) = 1219.2
    c: DistanceY(g1,g1) = 2438.4
FEATURE [PartDesign::Pad] Pad009
  Length = 2.032
  Length2 = 100
  Placement = pos=(0,0,0) rot=(0.57735,0.57735,0.57735;2.0944rad)
  Profile = -> Sketch009
  Type = 0
FEATURE [PartDesign::Body] Body003  label="4ftx8ft_Acrylic_Panel_001"
  Group = -> [Sketch009,Pad009]
  Origin = -> Origin003
  Placement = pos=(0.254,-20.5105,61.6585) rot=(0,0,1;0rad)
  Tip = -> Pad009
FEATURE [Sketcher::SketchObject] Sketch010
  MapMode = 5
  Placement = pos=(0,0,0) rot=(0.57735,0.57735,0.57735;2.0944rad)
  Support = -> [YZ_Plane004]
  sketch-geometry (4):
    g0: LineSegment StartX=0 StartY=0 StartZ=0 EndX=1219.2 EndY=0 EndZ=0
    g1: LineSegment StartX=1219.2 StartY=0 StartZ=0 EndX=1219.2 EndY=2438.4 EndZ=0
    g2: LineSegment StartX=1219.2 StartY=2438.4 StartZ=0 EndX=0 EndY=2438.4 EndZ=0
    g3: LineSegment StartX=0 StartY=2438.4 StartZ=0 EndX=0 EndY=0 EndZ=0
  constraints (11):
    c: Coincident(g0,g1)
    c: Coincident(g1,g2)
    c: Coincident(g2,g3)
    c: Coincident(g3,g0)
    c: Horizontal(g0)
    c: Horizontal(g2)
    c: Vertical(g1)
    c: Vertical(g3)
    c: Coincident(g0,g-1)
    c: DistanceX(g0,g0) = 1219.2
    c: DistanceY(g1,g1) = 2438.4
FEATURE [PartDesign::Pad] Pad010
  Length = 2.032
  Length2 = 100
  Placement = pos=(0,0,0) rot=(0.57735,0.57735,0.57735;2.0944rad)
  Profile = -> Sketch010
  Type = 0
FEATURE [PartDesign::Body] Body004  label="4ftx8ft_Acrylic_Panel_002"
  Group = -> [Sketch010,Pad010]
  Origin = -> Origin004
  Placement = pos=(0.254,1219.2,61.6585) rot=(0,0,1;0rad)
  Tip = -> Pad010
FEATURE [Sketcher::SketchObject] Sketch011
  MapMode = 5
  Placement = pos=(0,0,0) rot=(0.57735,0.57735,0.57735;2.0944rad)
  Support = -> [YZ_Plane005]
  sketch-geometry (4):
    g0: LineSegment StartX=0 StartY=0 StartZ=0 EndX=1219.2 EndY=0 EndZ=0
    g1: LineSegment StartX=1219.2 StartY=0 StartZ=0 EndX=1219.2 EndY=2438.4 EndZ=0
    g2: LineSegment StartX=1219.2 StartY=2438.4 StartZ=0 EndX=0 EndY=2438.4 EndZ=0
    g3: LineSegment StartX=0 StartY=2438.4 StartZ=0 EndX=0 EndY=0 EndZ=0
  constraints (11):
    c: Coincident(g0,g1)
    c: Coincident(g1,g2)
    c: Coincident(g2,g3)
    c: Coincident(g3,g0)
    c: Horizontal(g0)
    c: Horizontal(g2)
    c: Vertical(g1)
    c: Vertical(g3)
    c: Coincident(g0,g-1)
    c: DistanceX(g0,g0) = 1219.2
    c: DistanceY(g1,g1) = 2438.4
FEATURE [PartDesign::Pad] Pad011
  Length = 2.032
  Length2 = 100
  Placement = pos=(0,0,0) rot=(0.57735,0.57735,0.57735;2.0944rad)
  Profile = -> Sketch011
  Type = 0
FEATURE [PartDesign::Body] Body005  label="4ftx8ft_Acrylic_Panel_003"
  Group = -> [Sketch011,Pad011]
  Origin = -> Origin005
  Placement = pos=(-2524.25,-20.5105,61.6585) rot=(0,0,1;0rad)
  Tip = -> Pad011
FEATURE [Sketcher::SketchObject] Sketch012
  MapMode = 5
  Placement = pos=(0,0,0) rot=(0.57735,0.57735,0.57735;2.0944rad)
  Support = -> [YZ_Plane006]
  sketch-geometry (4):
    g0: LineSegment StartX=0 StartY=0 StartZ=0 EndX=1219.2 EndY=0 EndZ=0
    g1: LineSegment StartX=1219.2 StartY=0 StartZ=0 EndX=1219.2 EndY=2438.4 EndZ=0
    g2: LineSegment StartX=1219.2 StartY=2438.4 StartZ=0 EndX=0 EndY=2438.4 EndZ=0
    g3: LineSegment StartX=0 StartY=2438.4 StartZ=0 EndX=0 EndY=0 EndZ=0
  constraints (11):
    c: Coincident(g0,g1)
    c: Coincident(g1,g2)
    c: Coincident(g2,g3)
    c: Coincident(g3,g0)
    c: Horizontal(g0)
    c: Horizontal(g2)
    c: Vertical(g1)
    c: Vertical(g3)
    c: Coincident(g0,g-1)
    c: DistanceX(g0,g0) = 1219.2
    c: DistanceY(g1,g1) = 2438.4
FEATURE [PartDesign::Pad] Pad012
  Length = 2.032
  Length2 = 100
  Placement = pos=(0,0,0) rot=(0.57735,0.57735,0.57735;2.0944rad)
  Profile = -> Sketch012
  Type = 0
FEATURE [PartDesign::Body] Body006  label="4ftx8ft_Acrylic_Panel_004"
  Group = -> [Sketch012,Pad012]
  Origin = -> Origin006
  Placement = pos=(-2524.25,1219.2,61.6585) rot=(0,0,1;0rad)
  Tip = -> Pad012
FEATURE [Sketcher::SketchObject] Sketch013
  MapMode = 5
  Placement = pos=(0,0,0) rot=(0.57735,0.57735,0.57735;2.0944rad)
  Support = -> [YZ_Plane007]
  sketch-geometry (4):
    g0: LineSegment StartX=0 StartY=0 StartZ=0 EndX=1219.2 EndY=0 EndZ=0
    g1: LineSegment StartX=1219.2 StartY=0 StartZ=0 EndX=1219.2 EndY=2438.4 EndZ=0
    g2: LineSegment StartX=1219.2 StartY=2438.4 StartZ=0 EndX=0 EndY=2438.4 EndZ=0
    g3: LineSegment StartX=0 StartY=2438.4 StartZ=0 EndX=0 EndY=0 EndZ=0
  constraints (11):
    c: Coincident(g0,g1)
    c: Coincident(g1,g2)
    c: Coincident(g2,g3)
    c: Coincident(g3,g0)
    c: Horizontal(g0)
    c: Horizontal(g2)
    c: Vertical(g1)
    c: Vertical(g3)
    c: Coincident(g0,g-1)
    c: DistanceX(g0,g0) = 1219.2
    c: DistanceY(g1,g1) = 2438.4
FEATURE [PartDesign::Pad] Pad013
  Length = 2.032
  Length2 = 100
  Placement = pos=(0,0,0) rot=(0.57735,0.57735,0.57735;2.0944rad)
  Profile = -> Sketch013
  Type = 0
FEATURE [PartDesign::Body] Body007  label="4ftx8ft_Acrylic_Panel_005"
  Group = -> [Sketch013,Pad013]
  Origin = -> Origin007
  Placement = pos=(-30.5117,2479.42,61.6585) rot=(0,0,1;1.5708rad)
  Tip = -> Pad013
FEATURE [Sketcher::SketchObject] Sketch014
  MapMode = 5
  Placement = pos=(0,0,0) rot=(0.57735,0.57735,0.57735;2.0944rad)
  Support = -> [YZ_Plane008]
  sketch-geometry (4):
    g0: LineSegment StartX=0 StartY=0 StartZ=0 EndX=1219.2 EndY=0 EndZ=0
    g1: LineSegment StartX=1219.2 StartY=0 StartZ=0 EndX=1219.2 EndY=2438.4 EndZ=0
    g2: LineSegment StartX=1219.2 StartY=2438.4 StartZ=0 EndX=0 EndY=2438.4 EndZ=0
    g3: LineSegment StartX=0 StartY=2438.4 StartZ=0 EndX=0 EndY=0 EndZ=0
  constraints (11):
    c: Coincident(g0,g1)
    c: Coincident(g1,g2)
    c: Coincident(g2,g3)
    c: Coincident(g3,g0)
    c: Horizontal(g0)
    c: Horizontal(g2)
    c: Vertical(g1)
    c: Vertical(g3)
    c: Coincident(g0,g-1)
    c: DistanceX(g0,g0) = 1219.2
    c: DistanceY(g1,g1) = 2438.4
FEATURE [PartDesign::Pad] Pad014
  Length = 2.032
  Length2 = 100
  Placement = pos=(0,0,0) rot=(0.57735,0.57735,0.57735;2.0944rad)
  Profile = -> Sketch014
  Type = 0
FEATURE [PartDesign::Body] Body008  label="4ftx8ft_Acrylic_Panel_006"
  Group = -> [Sketch014,Pad014]
  Origin = -> Origin008
  Placement = pos=(-1270.22,2479.42,61.6585) rot=(0,0,1;1.5708rad)
  Tip = -> Pad014
FEATURE [Sketcher::SketchObject] Sketch015
  MapMode = 5
  Placement = pos=(0,0,0) rot=(0.57735,0.57735,0.57735;2.0944rad)
  Support = -> [YZ_Plane009]
  sketch-geometry (4):
    g0: LineSegment StartX=0 StartY=0 StartZ=0 EndX=1219.2 EndY=0 EndZ=0
    g1: LineSegment StartX=1219.2 StartY=0 StartZ=0 EndX=1219.2 EndY=2438.4 EndZ=0
    g2: LineSegment StartX=1219.2 StartY=2438.4 StartZ=0 EndX=0 EndY=2438.4 EndZ=0
    g3: LineSegment StartX=0 StartY=2438.4 StartZ=0 EndX=0 EndY=0 EndZ=0
  constraints (11):
    c: Coincident(g0,g1)
    c: Coincident(g1,g2)
    c: Coincident(g2,g3)
    c: Coincident(g3,g0)
    c: Horizontal(g0)
    c: Horizontal(g2)
    c: Vertical(g1)
    c: Vertical(g3)
    c: Coincident(g0,g-1)
    c: DistanceX(g0,g0) = 1219.2
    c: DistanceY(g1,g1) = 2438.4
FEATURE [PartDesign::Pad] Pad015
  Length = 2.032
  Length2 = 100
  Placement = pos=(0,0,0) rot=(0.57735,0.57735,0.57735;2.0944rad)
  Profile = -> Sketch015
  Type = 0
FEATURE [PartDesign::Body] Body009  label="4ftx8ft_Acrylic_Panel_007"
  Group = -> [Sketch015,Pad015]
  Origin = -> Origin009
  Placement = pos=(-609.346,-1260.22,61.6585) rot=(0,0,1;0rad)
  Tip = -> Pad015
FEATURE [Sketcher::SketchObject] Sketch016
  MapMode = 5
  Placement = pos=(0,0,0) rot=(0.57735,0.57735,0.57735;2.0944rad)
  Support = -> [YZ_Plane010]
  sketch-geometry (4):
    g0: LineSegment StartX=0 StartY=0 StartZ=0 EndX=1219.2 EndY=0 EndZ=0
    g1: LineSegment StartX=1219.2 StartY=0 StartZ=0 EndX=1219.2 EndY=2438.4 EndZ=0
    g2: LineSegment StartX=1219.2 StartY=2438.4 StartZ=0 EndX=0 EndY=2438.4 EndZ=0
    g3: LineSegment StartX=0 StartY=2438.4 StartZ=0 EndX=0 EndY=0 EndZ=0
  constraints (11):
    c: Coincident(g0,g1)
    c: Coincident(g1,g2)
    c: Coincident(g2,g3)
    c: Coincident(g3,g0)
    c: Horizontal(g0)
    c: Horizontal(g2)
    c: Vertical(g1)
    c: Vertical(g3)
    c: Coincident(g0,g-1)
    c: DistanceX(g0,g0) = 1219.2
    c: DistanceY(g1,g1) = 2438.4
FEATURE [PartDesign::Pad] Pad016
  Length = 2.032
  Length2 = 100
  Placement = pos=(0,0,0) rot=(0.57735,0.57735,0.57735;2.0944rad)
  Profile = -> Sketch016
  Type = 0
FEATURE [PartDesign::Body] Body010  label="4ftx8ft_Acrylic_Panel_008"
  Group = -> [Sketch016,Pad016]
  Origin = -> Origin010
  Placement = pos=(-1913.64,-1260.22,61.6585) rot=(0,0,1;0rad)
  Tip = -> Pad016
FEATURE [Sketcher::SketchObject] Sketch017
  MapMode = 5
  Placement = pos=(0,0,0) rot=(0.57735,0.57735,0.57735;2.0944rad)
  Support = -> [YZ_Plane011]
  sketch-geometry (4):
    g0: LineSegment StartX=0 StartY=0 StartZ=0 EndX=1219.2 EndY=0 EndZ=0
    g1: LineSegment StartX=1219.2 StartY=0 StartZ=0 EndX=1219.2 EndY=2438.4 EndZ=0
    g2: LineSegment StartX=1219.2 StartY=2438.4 StartZ=0 EndX=0 EndY=2438.4 EndZ=0
    g3: LineSegment StartX=0 StartY=2438.4 StartZ=0 EndX=0 EndY=0 EndZ=0
  constraints (11):
    c: Coincident(g0,g1)
    c: Coincident(g1,g2)
    c: Coincident(g2,g3)
    c: Coincident(g3,g0)
    c: Horizontal(g0)
    c: Horizontal(g2)
    c: Vertical(g1)
    c: Vertical(g3)
    c: Coincident(g0,g-1)
    c: DistanceX(g0,g0) = 1219.2
    c: DistanceY(g1,g1) = 2438.4
FEATURE [PartDesign::Pad] Pad017
  Length = 2.032
  Length2 = 100
  Placement = pos=(0,0,0) rot=(0.57735,0.57735,0.57735;2.0944rad)
  Profile = -> Sketch017
  Type = 0
FEATURE [PartDesign::Body] Body011  label="4ftx8ft_Acrylic_Panel_009"
  Group = -> [Sketch017,Pad017]
  Origin = -> Origin011
  Placement = pos=(-45.8946,-20.5105,2500.82) rot=(0,-1,0;1.5708rad)
  Tip = -> Pad017
FEATURE [Sketcher::SketchObject] Sketch018
  MapMode = 5
  Placement = pos=(0,0,0) rot=(0.57735,0.57735,0.57735;2.0944rad)
  Support = -> [YZ_Plane012]
  sketch-geometry (4):
    g0: LineSegment StartX=0 StartY=0 StartZ=0 EndX=1219.2 EndY=0 EndZ=0
    g1: LineSegment StartX=1219.2 StartY=0 StartZ=0 EndX=1219.2 EndY=1219.2 EndZ=0
    g2: LineSegment StartX=1219.2 StartY=1219.2 StartZ=0 EndX=0 EndY=1219.2 EndZ=0
    g3: LineSegment StartX=0 StartY=1219.2 StartZ=0 EndX=0 EndY=0 EndZ=0
  constraints (11):
    c: Coincident(g0,g1)
    c: Coincident(g1,g2)
    c: Coincident(g2,g3)
    c: Coincident(g3,g0)
    c: Horizontal(g0)
    c: Horizontal(g2)
    c: Vertical(g1)
    c: Vertical(g3)
    c: Coincident(g0,g-1)
    c: DistanceX(g0,g0) = 1219.2
    c: DistanceY(g1,g1) = 1219.2
FEATURE [PartDesign::Pad] Pad018
  Length = 2.032
  Length2 = 100
  Placement = pos=(0,0,0) rot=(0.57735,0.57735,0.57735;2.0944rad)
  Profile = -> Sketch018
  Type = 0
FEATURE [PartDesign::Body] Body012  label="4ftx4ft_Acrylic_Panel_001"
  Group = -> [Sketch018,Pad018]
  Origin = -> Origin012
  Placement = pos=(-650.367,-1260.22,2500.82) rot=(0,-1,0;1.5708rad)
  Tip = -> Pad018
FEATURE [Sketcher::SketchObject] Sketch019
  MapMode = 5
  Placement = pos=(0,0,0) rot=(0.57735,0.57735,0.57735;2.0944rad)
  Support = -> [YZ_Plane013]
  sketch-geometry (4):
    g0: LineSegment StartX=0 StartY=0 StartZ=0 EndX=609.6 EndY=0 EndZ=0
    g1: LineSegment StartX=609.6 StartY=0 StartZ=0 EndX=609.6 EndY=2438.4 EndZ=0
    g2: LineSegment StartX=609.6 StartY=2438.4 StartZ=0 EndX=0 EndY=2438.4 EndZ=0
    g3: LineSegment StartX=0 StartY=2438.4 StartZ=0 EndX=0 EndY=0 EndZ=0
  constraints (11):
    c: Coincident(g0,g1)
    c: Coincident(g1,g2)
    c: Coincident(g2,g3)
    c: Coincident(g3,g0)
    c: Horizontal(g0)
    c: Horizontal(g2)
    c: Vertical(g1)
    c: Vertical(g3)
    c: Coincident(g0,g-1)
    c: DistanceX(g0,g0) = 609.6
    c: DistanceY(g1,g1) = 2438.4
FEATURE [PartDesign::Pad] Pad019
  Length = 2.032
  Length2 = 100
  Placement = pos=(0,0,0) rot=(0.57735,0.57735,0.57735;2.0944rad)
  Profile = -> Sketch019
  Type = 0
FEATURE [PartDesign::Body] Body013  label="2ftx8ft_Acrylic_Panel_001"
  Group = -> [Sketch019,Pad019]
  Origin = -> Origin013
  Placement = pos=(-609.346,-41.021,61.6585) rot=(0,0,-1;1.5708rad)
  Tip = -> Pad019
FEATURE [Sketcher::SketchObject] Sketch020
  MapMode = 5
  Placement = pos=(0,0,0) rot=(0.57735,0.57735,0.57735;2.0944rad)
  Support = -> [YZ_Plane014]
  sketch-geometry (4):
    g0: LineSegment StartX=0 StartY=0 StartZ=0 EndX=609.6 EndY=0 EndZ=0
    g1: LineSegment StartX=609.6 StartY=0 StartZ=0 EndX=609.6 EndY=2438.4 EndZ=0
    g2: LineSegment StartX=609.6 StartY=2438.4 StartZ=0 EndX=0 EndY=2438.4 EndZ=0
    g3: LineSegment StartX=0 StartY=2438.4 StartZ=0 EndX=0 EndY=0 EndZ=0
  constraints (11):
    c: Coincident(g0,g1)
    c: Coincident(g1,g2)
    c: Coincident(g2,g3)
    c: Coincident(g3,g0)
    c: Horizontal(g0)
    c: Horizontal(g2)
    c: Vertical(g1)
    c: Vertical(g3)
    c: Coincident(g0,g-1)
    c: DistanceX(g0,g0) = 609.6
    c: DistanceY(g1,g1) = 2438.4
FEATURE [PartDesign::Pad] Pad020
  Length = 2.032
  Length2 = 100
  Placement = pos=(0,0,0) rot=(0.57735,0.57735,0.57735;2.0944rad)
  Profile = -> Sketch020
  Type = 0
FEATURE [PartDesign::Body] Body014  label="2ftx8ft_Acrylic_Panel_002"
  Group = -> [Sketch020,Pad020]
  Origin = -> Origin014
  Placement = pos=(-2520.19,-41.021,61.6585) rot=(0,0,-1;1.5708rad)
  Tip = -> Pad020
FEATURE [Sketcher::SketchObject] Sketch021
  MapMode = 5
  Placement = pos=(0,0,0) rot=(0.57735,0.57735,0.57735;2.0944rad)
  Support = -> [YZ_Plane015]
  sketch-geometry (4):
    g0: LineSegment StartX=0 StartY=0 StartZ=0 EndX=1219.2 EndY=0 EndZ=0
    g1: LineSegment StartX=1219.2 StartY=0 StartZ=0 EndX=1219.2 EndY=304.8 EndZ=0
    g2: LineSegment StartX=1219.2 StartY=304.8 StartZ=0 EndX=0 EndY=304.8 EndZ=0
    g3: LineSegment StartX=0 StartY=304.8 StartZ=0 EndX=0 EndY=0 EndZ=0
  constraints (11):
    c: Coincident(g0,g1)
    c: Coincident(g1,g2)
    c: Coincident(g2,g3)
    c: Coincident(g3,g0)
    c: Horizontal(g0)
    c: Horizontal(g2)
    c: Vertical(g1)
    c: Vertical(g3)
    c: Coincident(g0,g-1)
    c: DistanceX(g0,g0) = 1219.2
    c: DistanceY(g1,g1) = 304.8
FEATURE [PartDesign::Pad] Pad021
  Length = 2.032
  Length2 = 100
  Placement = pos=(0,0,0) rot=(0.57735,0.57735,0.57735;2.0944rad)
  Profile = -> Sketch021
  Type = 0
FEATURE [PartDesign::Body] Body015  label="4ftx10in_Acrylic_Panel_001"
  Group = -> [Sketch021,Pad021]
  Origin = -> Origin015
  Placement = pos=(-4.87363,1219.2,2500.82) rot=(0,-1,0;1.5708rad)
  Tip = -> Pad021
FEATURE [Sketcher::SketchObject] Sketch022
  MapMode = 5
  Placement = pos=(0,0,0) rot=(0.57735,0.57735,0.57735;2.0944rad)
  Support = -> [YZ_Plane016]
  sketch-geometry (4):
    g0: LineSegment StartX=0 StartY=0 StartZ=0 EndX=1219.2 EndY=0 EndZ=0
    g1: LineSegment StartX=1219.2 StartY=0 StartZ=0 EndX=1219.2 EndY=304.8 EndZ=0
    g2: LineSegment StartX=1219.2 StartY=304.8 StartZ=0 EndX=0 EndY=304.8 EndZ=0
    g3: LineSegment StartX=0 StartY=304.8 StartZ=0 EndX=0 EndY=0 EndZ=0
  constraints (11):
    c: Coincident(g0,g1)
    c: Coincident(g1,g2)
    c: Coincident(g2,g3)
    c: Coincident(g3,g0)
    c: Horizontal(g0)
    c: Horizontal(g2)
    c: Vertical(g1)
    c: Vertical(g3)
    c: Coincident(g0,g-1)
    c: DistanceX(g0,g0) = 1219.2
    c: DistanceY(g1,g1) = 304.8
FEATURE [PartDesign::Pad] Pad022
  Length = 2.032
  Length2 = 100
  Placement = pos=(0,0,0) rot=(0.57735,0.57735,0.57735;2.0944rad)
  Profile = -> Sketch022
  Type = 0
FEATURE [PartDesign::Body] Body016  label="4ftx10in_Acrylic_Panel_002"
  Group = -> [Sketch022,Pad022]
  Origin = -> Origin016
  Placement = pos=(-2209.75,1219.2,2500.82) rot=(0,-1,0;1.5708rad)
  Tip = -> Pad022
FEATURE [Sketcher::SketchObject] Sketch023
  MapMode = 5
  Support = -> [XY_Plane017]
  sketch-geometry (4):
    g0: LineSegment StartX=0 StartY=0 StartZ=0 EndX=-609.6 EndY=0 EndZ=0
    g1: LineSegment StartX=-609.6 StartY=0 StartZ=0 EndX=-609.6 EndY=2438.4 EndZ=0
    g2: LineSegment StartX=-609.6 StartY=2438.4 StartZ=0 EndX=0 EndY=2438.4 EndZ=0
    g3: LineSegment StartX=0 StartY=2438.4 StartZ=0 EndX=0 EndY=0 EndZ=0
  constraints (11):
    c: Coincident(g0,g1)
    c: Coincident(g1,g2)
    c: Coincident(g2,g3)
    c: Coincident(g3,g0)
    c: Horizontal(g0)
    c: Horizontal(g2)
    c: Vertical(g1)
    c: Vertical(g3)
    c: Coincident(g0,g-1)
    c: DistanceX(g2,g2) = 609.6
    c: DistanceY(g1,g1) = 2438.4
FEATURE [PartDesign::Pad] Pad023
  Length = 25.4
  Length2 = 100
  Profile = -> Sketch023
  Type = 0
FEATURE [PartDesign::Body] Body017  label="Bench_Top"
  Group = -> [Sketch023,Pad023]
  Origin = -> Origin017
  Placement = pos=(-41.021,0,975.741) rot=(0,0,1;0rad)
  Tip = -> Pad023
FEATURE [Part::Feature] Part__Feature089  label="Small_Tee_Bracket_33125T466_005"
  Placement = pos=(-558.324,182.69,931.866) rot=(0,0,-1;1.5708rad)
  shape: bbox 88.9 x 88.9 x 6.35 mm, 14 faces (baked)
FEATURE [Part::Feature] Part__Feature090  label="Small_Tee_Bracket_33125T466_006"
  Placement = pos=(-92.2973,182.689,931.866) rot=(0,0,1;1.5708rad)
  shape: bbox 88.9 x 88.9 x 6.35 mm, 14 faces (baked)
FEATURE [Part::Feature] Part__Feature091  label="2ft_Strut_Channel_3310T475_005"
  Placement = pos=(-609.6,182.563,976.312) rot=(0,-1,0;1.5708rad)
  shape: bbox 609.6 x 41.28 x 41.28 mm, 92 faces (baked)
FEATURE [Part::Feature] Part__Feature092  label="Small_Tee_Bracket_33125T466_007"
  Placement = pos=(-558.324,2255.71,931.866) rot=(0,0,-1;1.5708rad)
  shape: bbox 88.9 x 88.9 x 6.35 mm, 14 faces (baked)
FEATURE [Part::Feature] Part__Feature093  label="Small_Tee_Bracket_33125T466_008"
  Placement = pos=(-92.2972,2255.71,931.866) rot=(0,0,1;1.5708rad)
  shape: bbox 88.9 x 88.9 x 6.35 mm, 14 faces (baked)
FEATURE [Part::Feature] Part__Feature094  label="2ft_Strut_Channel_3310T475_006"
  Placement = pos=(-609.6,2255.58,976.312) rot=(0,-1,0;1.5708rad)
  shape: bbox 609.6 x 41.28 x 41.28 mm, 92 faces (baked)
FEATURE [Part::Feature] Part__Feature095  label="Shelf_Bracket_8p5in_3200T53_001"
  Placement = pos=(-1756.21,-20.5105,1849.31) rot=(1,0,0;1.5708rad)
  shape: bbox 225.4 x 41.15 x 118.7 mm, 23 faces (baked)
FEATURE [Part::Feature] Part__Feature096  label="Shelf_Bracket_8p5in_3200T53_002"
  Placement = pos=(-1756.21,-1280.73,1849.31) rot=(1,0,0;1.5708rad)
  shape: bbox 225.4 x 41.15 x 118.7 mm, 23 faces (baked)
FEATURE [Part::Feature] Part__Feature097  label="Shelf_Bracket_8p5in_3200T53_003"
  Placement = pos=(-1756.21,-1280.73,1544.51) rot=(1,0,0;1.5708rad)
  shape: bbox 225.4 x 41.15 x 118.7 mm, 23 faces (baked)
FEATURE [Part::Feature] Part__Feature098  label="Shelf_Bracket_8p5in_3200T53_004"
  Placement = pos=(-1756.21,-20.5105,1544.51) rot=(1,0,0;1.5708rad)
  shape: bbox 225.4 x 41.15 x 118.7 mm, 23 faces (baked)
FEATURE [Sketcher::SketchObject] Sketch024
  MapMode = 5
  Support = -> [XY_Plane018]
  sketch-geometry (4):
    g0: LineSegment StartX=0 StartY=0 StartZ=0 EndX=215.9 EndY=0 EndZ=0
    g1: LineSegment StartX=215.9 StartY=0 StartZ=0 EndX=215.9 EndY=1303.02 EndZ=0
    g2: LineSegment StartX=215.9 StartY=1303.02 StartZ=0 EndX=0 EndY=1303.02 EndZ=0
    g3: LineSegment StartX=0 StartY=1303.02 StartZ=0 EndX=0 EndY=0 EndZ=0
  constraints (11):
    c: Coincident(g0,g1)
    c: Coincident(g1,g2)
    c: Coincident(g2,g3)
    c: Coincident(g3,g0)
    c: Horizontal(g0)
    c: Horizontal(g2)
    c: Vertical(g1)
    c: Vertical(g3)
    c: Coincident(g0,g-1)
    c: DistanceX(g0,g0) = 215.9
    c: DistanceY(g1,g1) = 1303.02
FEATURE [PartDesign::Pad] Pad024
  Length = 12.7
  Length2 = 100
  Profile = -> Sketch024
  Type = 0
FEATURE [PartDesign::Body] Body018  label="Shelf_8p5inx51p23in_001"
  Group = -> [Sketch024,Pad024]
  Origin = -> Origin018
  Placement = pos=(-1868.81,-1301.24,1849.76) rot=(0,0,1;0rad)
  Tip = -> Pad024
FEATURE [Sketcher::SketchObject] Sketch025
  MapMode = 5
  Support = -> [XY_Plane019]
  sketch-geometry (4):
    g0: LineSegment StartX=0 StartY=0 StartZ=0 EndX=215.9 EndY=0 EndZ=0
    g1: LineSegment StartX=215.9 StartY=0 StartZ=0 EndX=215.9 EndY=1303.02 EndZ=0
    g2: LineSegment StartX=215.9 StartY=1303.02 StartZ=0 EndX=0 EndY=1303.02 EndZ=0
    g3: LineSegment StartX=0 StartY=1303.02 StartZ=0 EndX=0 EndY=0 EndZ=0
  constraints (11):
    c: Coincident(g0,g1)
    c: Coincident(g1,g2)
    c: Coincident(g2,g3)
    c: Coincident(g3,g0)
    c: Horizontal(g0)
    c: Horizontal(g2)
    c: Vertical(g1)
    c: Vertical(g3)
    c: Coincident(g0,g-1)
    c: DistanceX(g0,g0) = 215.9
    c: DistanceY(g1,g1) = 1303.02
FEATURE [PartDesign::Pad] Pad025
  Length = 12.7
  Length2 = 100
  Profile = -> Sketch025
  Type = 0
FEATURE [PartDesign::Body] Body019  label="Shelf_8p5inx51p23in_002"
  Group = -> [Sketch025,Pad025]
  Origin = -> Origin019
  Placement = pos=(-1868.81,-1301.24,1544.96) rot=(0,0,1;0rad)
  Tip = -> Pad025
FEATURE [Sketcher::SketchObject] Sketch026
  MapMode = 5
  Placement = pos=(0,0,0) rot=(0.57735,0.57735,0.57735;2.0944rad)
  Support = -> [YZ_Plane020]
  sketch-geometry (4):
    g0: LineSegment StartX=0 StartY=0 StartZ=0 EndX=304.8 EndY=0 EndZ=0
    g1: LineSegment StartX=304.8 StartY=0 StartZ=0 EndX=304.8 EndY=2438.4 EndZ=0
    g2: LineSegment StartX=304.8 StartY=2438.4 StartZ=0 EndX=0 EndY=2438.4 EndZ=0
    g3: LineSegment StartX=0 StartY=2438.4 StartZ=0 EndX=0 EndY=0 EndZ=0
  constraints (11):
    c: Coincident(g0,g1)
    c: Coincident(g1,g2)
    c: Coincident(g2,g3)
    c: Coincident(g3,g0)
    c: Horizontal(g0)
    c: Horizontal(g2)
    c: Vertical(g1)
    c: Vertical(g3)
    c: Coincident(g0,g-1)
    c: DistanceX(g0,g0) = 304.8
    c: DistanceY(g1,g1) = 2438.4
FEATURE [PartDesign::Pad] Pad026
  Length = 2.032
  Length2 = 100
  Placement = pos=(0,0,0) rot=(0.57735,0.57735,0.57735;2.0944rad)
  Profile = -> Sketch026
  Type = 0
FEATURE [PartDesign::Body] Body020  label="Vinyl_Flap_1ftx8ft_001"
  Group = -> [Sketch026,Pad026]
  Origin = -> Origin020
  Placement = pos=(-955.675,-1302.26,61.6585) rot=(0,0,-1;1.5708rad)
  Tip = -> Pad026
FEATURE [Sketcher::SketchObject] Sketch027
  MapMode = 5
  Placement = pos=(0,0,0) rot=(0.57735,0.57735,0.57735;2.0944rad)
  Support = -> [YZ_Plane021]
  sketch-geometry (4):
    g0: LineSegment StartX=0 StartY=0 StartZ=0 EndX=304.8 EndY=0 EndZ=0
    g1: LineSegment StartX=304.8 StartY=0 StartZ=0 EndX=304.8 EndY=2438.4 EndZ=0
    g2: LineSegment StartX=304.8 StartY=2438.4 StartZ=0 EndX=0 EndY=2438.4 EndZ=0
    g3: LineSegment StartX=0 StartY=2438.4 StartZ=0 EndX=0 EndY=0 EndZ=0
  constraints (11):
    c: Coincident(g0,g1)
    c: Coincident(g1,g2)
    c: Coincident(g2,g3)
    c: Coincident(g3,g0)
    c: Horizontal(g0)
    c: Horizontal(g2)
    c: Vertical(g1)
    c: Vertical(g3)
    c: Coincident(g0,g-1)
    c: DistanceX(g0,g0) = 304.8
    c: DistanceY(g1,g1) = 2438.4
FEATURE [PartDesign::Pad] Pad027
  Length = 2.032
  Length2 = 100
  Placement = pos=(0,0,0) rot=(0.57735,0.57735,0.57735;2.0944rad)
  Profile = -> Sketch027
  Type = 0
FEATURE [PartDesign::Body] Body021  label="Vinyl_Flap_1ftx8ft_002"
  Group = -> [Sketch027,Pad027]
  Origin = -> Origin021
  Placement = pos=(-1260.47,-1302.26,61.6585) rot=(0,0,-1;1.5708rad)
  Tip = -> Pad027
FEATURE [Sketcher::SketchObject] Sketch028
  MapMode = 5
  Placement = pos=(0,0,0) rot=(0.57735,0.57735,0.57735;2.0944rad)
  Support = -> [YZ_Plane022]
  sketch-geometry (4):
    g0: LineSegment StartX=0 StartY=0 StartZ=0 EndX=304.8 EndY=0 EndZ=0
    g1: LineSegment StartX=304.8 StartY=0 StartZ=0 EndX=304.8 EndY=2438.4 EndZ=0
    g2: LineSegment StartX=304.8 StartY=2438.4 StartZ=0 EndX=0 EndY=2438.4 EndZ=0
    g3: LineSegment StartX=0 StartY=2438.4 StartZ=0 EndX=0 EndY=0 EndZ=0
  constraints (11):
    c: Coincident(g0,g1)
    c: Coincident(g1,g2)
    c: Coincident(g2,g3)
    c: Coincident(g3,g0)
    c: Horizontal(g0)
    c: Horizontal(g2)
    c: Vertical(g1)
    c: Vertical(g3)
    c: Coincident(g0,g-1)
    c: DistanceX(g0,g0) = 304.8
    c: DistanceY(g1,g1) = 2438.4
FEATURE [PartDesign::Pad] Pad028
  Length = 2.032
  Length2 = 100
  Placement = pos=(0,0,0) rot=(0.57735,0.57735,0.57735;2.0944rad)
  Profile = -> Sketch028
  Type = 0
FEATURE [PartDesign::Body] Body022  label="Vinyl_Flap_1ftx8ft_003"
  Group = -> [Sketch028,Pad028]
  Origin = -> Origin022
  Placement = pos=(-1565.27,-1302.26,61.6585) rot=(0,0,-1;1.5708rad)
  Tip = -> Pad028
FEATURE [Sketcher::SketchObject] Sketch029
  MapMode = 5
  Placement = pos=(0,0,0) rot=(0.57735,0.57735,0.57735;2.0944rad)
  Support = -> [YZ_Plane023]
  sketch-geometry (4):
    g0: LineSegment StartX=0 StartY=0 StartZ=0 EndX=304.8 EndY=0 EndZ=0
    g1: LineSegment StartX=304.8 StartY=0 StartZ=0 EndX=304.8 EndY=2438.4 EndZ=0
    g2: LineSegment StartX=304.8 StartY=2438.4 StartZ=0 EndX=0 EndY=2438.4 EndZ=0
    g3: LineSegment StartX=0 StartY=2438.4 StartZ=0 EndX=0 EndY=0 EndZ=0
  constraints (11):
    c: Coincident(g0,g1)
    c: Coincident(g1,g2)
    c: Coincident(g2,g3)
    c: Coincident(g3,g0)
    c: Horizontal(g0)
    c: Horizontal(g2)
    c: Vertical(g1)
    c: Vertical(g3)
    c: Coincident(g0,g-1)
    c: DistanceX(g0,g0) = 304.8
    c: DistanceY(g1,g1) = 2438.4
FEATURE [PartDesign::Pad] Pad029
  Length = 2.032
  Length2 = 100
  Placement = pos=(0,0,0) rot=(0.57735,0.57735,0.57735;2.0944rad)
  Profile = -> Sketch029
  Type = 0
FEATURE [PartDesign::Body] Body023  label="Vinyl_Flap_1ftx8ft_004"
  Group = -> [Sketch029,Pad029]
  Origin = -> Origin023
  Placement = pos=(-1870.07,-1302.26,61.6585) rot=(0,0,-1;1.5708rad)
  Tip = -> Pad029
FEATURE [Sketcher::SketchObject] Sketch030
  MapMode = 5
  Placement = pos=(0,0,0) rot=(0.57735,0.57735,0.57735;2.0944rad)
  Support = -> [YZ_Plane024]
  sketch-geometry (4):
    g0: LineSegment StartX=0 StartY=0 StartZ=0 EndX=304.8 EndY=0 EndZ=0
    g1: LineSegment StartX=304.8 StartY=0 StartZ=0 EndX=304.8 EndY=2438.4 EndZ=0
    g2: LineSegment StartX=304.8 StartY=2438.4 StartZ=0 EndX=0 EndY=2438.4 EndZ=0
    g3: LineSegment StartX=0 StartY=2438.4 StartZ=0 EndX=0 EndY=0 EndZ=0
  constraints (11):
    c: Coincident(g0,g1)
    c: Coincident(g1,g2)
    c: Coincident(g2,g3)
    c: Coincident(g3,g0)
    c: Horizontal(g0)
    c: Horizontal(g2)
    c: Vertical(g1)
    c: Vertical(g3)
    c: Coincident(g0,g-1)
    c: DistanceX(g0,g0) = 304.8
    c: DistanceY(g1,g1) = 2438.4
FEATURE [PartDesign::Pad] Pad030
  Length = 2.032
  Length2 = 100
  Placement = pos=(0,0,0) rot=(0.57735,0.57735,0.57735;2.0944rad)
  Profile = -> Sketch030
  Type = 0
FEATURE [PartDesign::Body] Body024  label="Vinyl_Flap_1ftx8ft_005"
  Group = -> [Sketch030,Pad030]
  Origin = -> Origin024
  Placement = pos=(-955.675,1.524,61.6585) rot=(0,0,-1;1.5708rad)
  Tip = -> Pad030
FEATURE [Sketcher::SketchObject] Sketch031
  MapMode = 5
  Placement = pos=(0,0,0) rot=(0.57735,0.57735,0.57735;2.0944rad)
  Support = -> [YZ_Plane025]
  sketch-geometry (4):
    g0: LineSegment StartX=0 StartY=0 StartZ=0 EndX=304.8 EndY=0 EndZ=0
    g1: LineSegment StartX=304.8 StartY=0 StartZ=0 EndX=304.8 EndY=2438.4 EndZ=0
    g2: LineSegment StartX=304.8 StartY=2438.4 StartZ=0 EndX=0 EndY=2438.4 EndZ=0
    g3: LineSegment StartX=0 StartY=2438.4 StartZ=0 EndX=0 EndY=0 EndZ=0
  constraints (11):
    c: Coincident(g0,g1)
    c: Coincident(g1,g2)
    c: Coincident(g2,g3)
    c: Coincident(g3,g0)
    c: Horizontal(g0)
    c: Horizontal(g2)
    c: Vertical(g1)
    c: Vertical(g3)
    c: Coincident(g0,g-1)
    c: DistanceX(g0,g0) = 304.8
    c: DistanceY(g1,g1) = 2438.4
FEATURE [PartDesign::Pad] Pad031
  Length = 2.032
  Length2 = 100
  Placement = pos=(0,0,0) rot=(0.57735,0.57735,0.57735;2.0944rad)
  Profile = -> Sketch031
  Type = 0
FEATURE [PartDesign::Body] Body025  label="Vinyl_Flap_1ftx8ft_006"
  Group = -> [Sketch031,Pad031]
  Origin = -> Origin025
  Placement = pos=(-1260.47,2.794,61.6585) rot=(0,0,-1;1.5708rad)
  Tip = -> Pad031
FEATURE [Sketcher::SketchObject] Sketch032
  MapMode = 5
  Placement = pos=(0,0,0) rot=(0.57735,0.57735,0.57735;2.0944rad)
  Support = -> [YZ_Plane026]
  sketch-geometry (4):
    g0: LineSegment StartX=0 StartY=0 StartZ=0 EndX=304.8 EndY=0 EndZ=0
    g1: LineSegment StartX=304.8 StartY=0 StartZ=0 EndX=304.8 EndY=2438.4 EndZ=0
    g2: LineSegment StartX=304.8 StartY=2438.4 StartZ=0 EndX=0 EndY=2438.4 EndZ=0
    g3: LineSegment StartX=0 StartY=2438.4 StartZ=0 EndX=0 EndY=0 EndZ=0
  constraints (11):
    c: Coincident(g0,g1)
    c: Coincident(g1,g2)
    c: Coincident(g2,g3)
    c: Coincident(g3,g0)
    c: Horizontal(g0)
    c: Horizontal(g2)
    c: Vertical(g1)
    c: Vertical(g3)
    c: Coincident(g0,g-1)
    c: DistanceX(g0,g0) = 304.8
    c: DistanceY(g1,g1) = 2438.4
FEATURE [PartDesign::Pad] Pad032
  Length = 2.032
  Length2 = 100
  Placement = pos=(0,0,0) rot=(0.57735,0.57735,0.57735;2.0944rad)
  Profile = -> Sketch032
  Type = 0
FEATURE [PartDesign::Body] Body026  label="Vinyl_Flap_1ftx8ft_007"
  Group = -> [Sketch032,Pad032]
  Origin = -> Origin026
  Placement = pos=(-1565.27,2.794,61.6585) rot=(0,0,-1;1.5708rad)
  Tip = -> Pad032
FEATURE [Sketcher::SketchObject] Sketch033
  MapMode = 5
  Placement = pos=(0,0,0) rot=(0.57735,0.57735,0.57735;2.0944rad)
  Support = -> [YZ_Plane027]
  sketch-geometry (4):
    g0: LineSegment StartX=0 StartY=0 StartZ=0 EndX=304.8 EndY=0 EndZ=0
    g1: LineSegment StartX=304.8 StartY=0 StartZ=0 EndX=304.8 EndY=2438.4 EndZ=0
    g2: LineSegment StartX=304.8 StartY=2438.4 StartZ=0 EndX=0 EndY=2438.4 EndZ=0
    g3: LineSegment StartX=0 StartY=2438.4 StartZ=0 EndX=0 EndY=0 EndZ=0
  constraints (11):
    c: Coincident(g0,g1)
    c: Coincident(g1,g2)
    c: Coincident(g2,g3)
    c: Coincident(g3,g0)
    c: Horizontal(g0)
    c: Horizontal(g2)
    c: Vertical(g1)
    c: Vertical(g3)
    c: Coincident(g0,g-1)
    c: DistanceX(g0,g0) = 304.8
    c: DistanceY(g1,g1) = 2438.4
FEATURE [PartDesign::Pad] Pad033
  Length = 2.032
  Length2 = 100
  Placement = pos=(0,0,0) rot=(0.57735,0.57735,0.57735;2.0944rad)
  Profile = -> Sketch033
  Type = 0
FEATURE [PartDesign::Body] Body027  label="Vinyl_Flap_1ftx8ft_008"
  Group = -> [Sketch033,Pad033]
  Origin = -> Origin027
  Placement = pos=(-1870.07,2.794,61.6585) rot=(0,0,-1;1.5708rad)
  Tip = -> Pad033
FEATURE [Part::Feature] Part__Feature099  label="4ft_Strut_Channel_3310T181_010"
  Placement = pos=(-650.875,-671.512,2459.29) rot=(0,-1,0;4.71239rad)
  shape: bbox 1219 x 41.28 x 41.28 mm, 152 faces (baked)
FEATURE [Part::Feature] Part__Feature100  label="Small_Tee_Bracket_33125T466_009"
  Placement = pos=(-698.692,-671.167,2455.87) rot=(0,0,1;1.5708rad)
  shape: bbox 88.9 x 88.9 x 6.35 mm, 14 faces (baked)
FEATURE [Part::Feature] Part__Feature101  label="Small_Tee_Bracket_33125T466_010"
  Placement = pos=(-1822.39,-671.167,2455.87) rot=(0,0,-1;1.5708rad)
  shape: bbox 88.9 x 88.9 x 6.35 mm, 14 faces (baked)
FEATURE [Mesh::Feature] Hanger_Large  label="Hanger_Large_001"
  Placement = pos=(-685.8,-673.1,2311.4) rot=(-0.707107,0,-0.707107;3.14159rad)
FEATURE [Mesh::Feature] Hanger_Large001  label="Hanger_Large_002"
  Placement = pos=(-736.6,-673.1,2311.4) rot=(-0.707107,0,-0.707107;3.14159rad)
FEATURE [Mesh::Feature] Hanger_Large002  label="Hanger_Large_003"
  Placement = pos=(-787.4,-673.1,2311.4) rot=(-0.707107,0,-0.707107;3.14159rad)
FEATURE [Sketcher::SketchObject] Sketch034
  MapMode = 5
  Placement = pos=(0,0,0) rot=(1,0,0;1.5708rad)
  Support = -> [XZ_Plane028]
  sketch-geometry (4):
    g0: LineSegment StartX=0 StartY=0 StartZ=0 EndX=3.175 EndY=0 EndZ=0
    g1: LineSegment StartX=3.175 StartY=0 StartZ=0 EndX=3.175 EndY=12.7 EndZ=0
    g2: LineSegment StartX=3.175 StartY=12.7 StartZ=0 EndX=0 EndY=12.7 EndZ=0
    g3: LineSegment StartX=0 StartY=12.7 StartZ=0 EndX=0 EndY=0 EndZ=0
  constraints (11):
    c: Coincident(g0,g1)
    c: Coincident(g1,g2)
    c: Coincident(g2,g3)
    c: Coincident(g3,g0)
    c: Horizontal(g0)
    c: Horizontal(g2)
    c: Vertical(g1)
    c: Vertical(g3)
    c: Coincident(g0,g-1)
    c: DistanceY(g1,g1) = 12.7
    c: DistanceX(g2,g2) = 3.175
FEATURE [PartDesign::Pad] Pad034
  Length = 1219.2
  Length2 = 100
  Placement = pos=(0,0,0) rot=(1,0,0;1.5708rad)
  Profile = -> Sketch034
  Reversed = true
  Type = 0
FEATURE [PartDesign::Body] Body028  label="Al_Bar_0p5inx0p125in_001"
  Group = -> [Sketch034,Pad034]
  Origin = -> Origin028
  Tip = -> Pad034
FEATURE [Part::Feature] Part__Feature102  label="4ft_Strut_Channel_3310T181_011"
  Placement = pos=(-1258.44,-1.42875,2459.29) rot=(-0.57735,-0.57735,0.57735;4.18879rad)
  shape: bbox 41.28 x 1219 x 41.28 mm, 152 faces (baked)
FEATURE [Part::Feature] Part__Feature104  label="Small_Tee_Bracket_33125T466_011"
  Placement = pos=(-1258.83,1130.71,2455.87) rot=(0,0,1;3.14159rad)
  shape: bbox 88.9 x 88.9 x 6.35 mm, 14 faces (baked)
FEATURE [Part::Feature] Part__Feature105  label="Small_Tee_Bracket_33125T466_012"
  Placement = pos=(-1258.83,47.502,2455.87) rot=(0,0,1;0rad)
  shape: bbox 88.9 x 88.9 x 6.35 mm, 14 faces (baked)
FEATURE [Sketcher::SketchObject] Sketch035
  MapMode = 5
  Placement = pos=(0,0,0) rot=(1,0,0;1.5708rad)
  Support = -> [XZ_Plane029]
  sketch-geometry (6):
    g0: LineSegment StartX=25.4 StartY=25.4 StartZ=0 EndX=25.4 EndY=0 EndZ=0
    g1: LineSegment StartX=25.4 StartY=0 StartZ=0 EndX=0 EndY=0 EndZ=0
    g2: LineSegment StartX=0 StartY=0 StartZ=0 EndX=0 EndY=3.175 EndZ=0
    g3: LineSegment StartX=0 StartY=3.175 StartZ=0 EndX=22.225 EndY=3.175 EndZ=0
    g4: LineSegment StartX=22.225 StartY=3.175 StartZ=0 EndX=22.225 EndY=25.4 EndZ=0
    g5: LineSegment StartX=22.225 StartY=25.4 StartZ=0 EndX=25.4 EndY=25.4 EndZ=0
  constraints (17):
    c: PointOnObject(g0,g-1)
    c: Vertical(g0)
    c: Coincident(g0,g1)
    c: Coincident(g1,g-1)
    c: Coincident(g1,g2)
    c: PointOnObject(g2,g-2)
    c: Coincident(g2,g3)
    c: Horizontal(g3)
    c: Coincident(g3,g4)
    c: Vertical(g4)
    c: Coincident(g4,g5)
    c: Coincident(g5,g0)
    c: Equal(g5,g2)
    c: Equal(g3,g4)
    c: Equal(g0,g1)
    c: DistanceX(g1,g1) = 25.4
    c: DistanceX(g5,g5) = 3.175
FEATURE [PartDesign::Pad] Pad035
  Length = 1219.2
  Length2 = 100
  Placement = pos=(0,0,0) rot=(1,0,0;1.5708rad)
  Profile = -> Sketch035
  Reversed = true
  Type = 0
FEATURE [Sketcher::SketchObject] Sketch036
  ExternalGeometry = -> [Pad035]
  MapMode = 5
  Placement = pos=(0,2.1e-15,3.175) rot=(0,0,1;3.14159rad)
  Support = -> [Pad035]
  sketch-geometry (8):
    g0: LineSegment StartX=0 StartY=-1219.2 StartZ=0 EndX=-22.225 EndY=-1219.2 EndZ=0
    g1: LineSegment StartX=-22.225 StartY=-1219.2 StartZ=0 EndX=-22.225 EndY=-1200.15 EndZ=0
    g2: LineSegment StartX=-22.225 StartY=-1200.15 StartZ=0 EndX=0 EndY=-1200.15 EndZ=0
    g3: LineSegment StartX=0 StartY=-1200.15 StartZ=0 EndX=0 EndY=-1219.2 EndZ=0
    g4: LineSegment StartX=0 StartY=0 StartZ=0 EndX=-22.225 EndY=0 EndZ=0
    g5: LineSegment StartX=-22.225 StartY=0 StartZ=0 EndX=-22.225 EndY=-19.05 EndZ=0
    g6: LineSegment StartX=-22.225 StartY=-19.05 StartZ=0 EndX=0 EndY=-19.05 EndZ=0
    g7: LineSegment StartX=0 StartY=-19.05 StartZ=0 EndX=0 EndY=0 EndZ=0
  constraints (22):
    c: Coincident(g0,g1)
    c: Coincident(g1,g2)
    c: Coincident(g2,g3)
    c: Coincident(g3,g0)
    c: Horizontal(g0)
    c: Horizontal(g2)
    c: Vertical(g1)
    c: Vertical(g3)
    c: Coincident(g0,g-4)
    c: PointOnObject(g1,g-3)
    c: DistanceY(g1,g1) = 19.05
    c: Coincident(g4,g5)
    c: Coincident(g5,g6)
    c: Coincident(g6,g7)
    c: Coincident(g7,g4)
    c: Horizontal(g4)
    c: Horizontal(g6)
    c: Vertical(g5)
    c: Vertical(g7)
    c: Coincident(g4,g-1)
    c: PointOnObject(g5,g-3)
    c: Distance(g5,g4) = 19.05
FEATURE [PartDesign::Pocket] Pocket
  BaseFeature = -> Pad035
  Length = 5
  Length2 = 100
  Placement = pos=(0,0,0) rot=(1,0,0;1.5708rad)
  Profile = -> Sketch036
  Type = 1
FEATURE [PartDesign::Body] Body029  label="Al_L-Channel_1inx0p125inx48in_001"
  Group = -> [Sketch035,Pad035,Sketch036,Pocket]
  Origin = -> Origin029
  Placement = pos=(-22.1361,-18.9763,173.037) rot=(0,0,1;0rad)
  Tip = -> Pocket
FEATURE [Sketcher::SketchObject] Sketch038
  MapMode = 5
  Placement = pos=(0,0,0) rot=(1,0,0;1.5708rad)
  Support = -> [XZ_Plane030]
  sketch-geometry (6):
    g0: LineSegment StartX=25.4 StartY=25.4 StartZ=0 EndX=25.4 EndY=0 EndZ=0
    g1: LineSegment StartX=25.4 StartY=0 StartZ=0 EndX=0 EndY=0 EndZ=0
    g2: LineSegment StartX=0 StartY=0 StartZ=0 EndX=0 EndY=3.175 EndZ=0
    g3: LineSegment StartX=0 StartY=3.175 StartZ=0 EndX=22.225 EndY=3.175 EndZ=0
    g4: LineSegment StartX=22.225 StartY=3.175 StartZ=0 EndX=22.225 EndY=25.4 EndZ=0
    g5: LineSegment StartX=22.225 StartY=25.4 StartZ=0 EndX=25.4 EndY=25.4 EndZ=0
  constraints (17):
    c: PointOnObject(g0,g-1)
    c: Vertical(g0)
    c: Coincident(g0,g1)
    c: Coincident(g1,g-1)
    c: Coincident(g1,g2)
    c: PointOnObject(g2,g-2)
    c: Coincident(g2,g3)
    c: Horizontal(g3)
    c: Coincident(g3,g4)
    c: Vertical(g4)
    c: Coincident(g4,g5)
    c: Coincident(g5,g0)
    c: Equal(g5,g2)
    c: Equal(g3,g4)
    c: Equal(g0,g1)
    c: DistanceX(g1,g1) = 25.4
    c: DistanceX(g5,g5) = 3.175
FEATURE [PartDesign::Pad] Pad036
  Length = 1258.57
  Length2 = 100
  Placement = pos=(0,0,0) rot=(1,0,0;1.5708rad)
  Profile = -> Sketch038
  Reversed = true
  Type = 0
FEATURE [Sketcher::SketchObject] Sketch037
  ExternalGeometry = -> [Pad036]
  MapMode = 5
  Placement = pos=(0,7e-16,3.175) rot=(0,0,1;3.14159rad)
  Support = -> [Pad036]
  sketch-geometry (8):
    g0: LineSegment StartX=0 StartY=-1258.57 StartZ=0 EndX=-22.225 EndY=-1258.57 EndZ=0
    g1: LineSegment StartX=-22.225 StartY=-1258.57 StartZ=0 EndX=-22.225 EndY=-1239.52 EndZ=0
    g2: LineSegment StartX=-22.225 StartY=-1239.52 StartZ=0 EndX=0 EndY=-1239.52 EndZ=0
    g3: LineSegment StartX=0 StartY=-1239.52 StartZ=0 EndX=0 EndY=-1258.57 EndZ=0
    g4: LineSegment StartX=0 StartY=0 StartZ=0 EndX=-22.225 EndY=0 EndZ=0
    g5: LineSegment StartX=-22.225 StartY=0 StartZ=0 EndX=-22.225 EndY=-19.05 EndZ=0
    g6: LineSegment StartX=-22.225 StartY=-19.05 StartZ=0 EndX=0 EndY=-19.05 EndZ=0
    g7: LineSegment StartX=0 StartY=-19.05 StartZ=0 EndX=0 EndY=0 EndZ=0
  constraints (22):
    c: Coincident(g0,g1)
    c: Coincident(g1,g2)
    c: Coincident(g2,g3)
    c: Coincident(g3,g0)
    c: Horizontal(g0)
    c: Horizontal(g2)
    c: Vertical(g1)
    c: Vertical(g3)
    c: Coincident(g0,g-4)
    c: PointOnObject(g1,g-3)
    c: DistanceY(g1,g1) = 19.05
    c: Coincident(g4,g5)
    c: Coincident(g5,g6)
    c: Coincident(g6,g7)
    c: Coincident(g7,g4)
    c: Horizontal(g4)
    c: Horizontal(g6)
    c: Vertical(g5)
    c: Vertical(g7)
    c: Coincident(g4,g-1)
    c: PointOnObject(g5,g-3)
    c: Distance(g5,g4) = 19.05
FEATURE [PartDesign::Pocket] Pocket001
  BaseFeature = -> Pad036
  Length = 5
  Length2 = 100
  Placement = pos=(0,0,0) rot=(1,0,0;1.5708rad)
  Profile = -> Sketch037
  Type = 1
FEATURE [PartDesign::Body] Body030  label="Al_L-Channel_1inx0p125inx49p55in_001"
  Group = -> [Sketch038,Pad036,Sketch037,Pocket001]
  Origin = -> Origin030
  Placement = pos=(-22.1361,1200.22,173.037) rot=(0,0,1;0rad)
  Tip = -> Pocket001
FEATURE [Sketcher::SketchObject] Sketch040
  MapMode = 5
  Placement = pos=(0,0,0) rot=(1,0,0;1.5708rad)
  Support = -> [XZ_Plane031]
  sketch-geometry (6):
    g0: LineSegment StartX=25.4 StartY=25.4 StartZ=0 EndX=25.4 EndY=0 EndZ=0
    g1: LineSegment StartX=25.4 StartY=0 StartZ=0 EndX=0 EndY=0 EndZ=0
    g2: LineSegment StartX=0 StartY=0 StartZ=0 EndX=0 EndY=3.175 EndZ=0
    g3: LineSegment StartX=0 StartY=3.175 StartZ=0 EndX=22.225 EndY=3.175 EndZ=0
    g4: LineSegment StartX=22.225 StartY=3.175 StartZ=0 EndX=22.225 EndY=25.4 EndZ=0
    g5: LineSegment StartX=22.225 StartY=25.4 StartZ=0 EndX=25.4 EndY=25.4 EndZ=0
  constraints (17):
    c: PointOnObject(g0,g-1)
    c: Vertical(g0)
    c: Coincident(g0,g1)
    c: Coincident(g1,g-1)
    c: Coincident(g1,g2)
    c: PointOnObject(g2,g-2)
    c: Coincident(g2,g3)
    c: Horizontal(g3)
    c: Coincident(g3,g4)
    c: Vertical(g4)
    c: Coincident(g4,g5)
    c: Coincident(g5,g0)
    c: Equal(g5,g2)
    c: Equal(g3,g4)
    c: Equal(g0,g1)
    c: DistanceX(g1,g1) = 25.4
    c: DistanceX(g5,g5) = 3.175
FEATURE [PartDesign::Pad] Pad037
  Length = 1219.2
  Length2 = 100
  Placement = pos=(0,0,0) rot=(1,0,0;1.5708rad)
  Profile = -> Sketch040
  Reversed = true
  Type = 0
FEATURE [Sketcher::SketchObject] Sketch039
  ExternalGeometry = -> [Pad037]
  MapMode = 5
  Placement = pos=(0,1.4e-15,3.175) rot=(0,0,1;3.14159rad)
  Support = -> [Pad037]
  sketch-geometry (8):
    g0: LineSegment StartX=0 StartY=-1219.2 StartZ=0 EndX=-22.225 EndY=-1219.2 EndZ=0
    g1: LineSegment StartX=-22.225 StartY=-1219.2 StartZ=0 EndX=-22.225 EndY=-1200.15 EndZ=0
    g2: LineSegment StartX=-22.225 StartY=-1200.15 StartZ=0 EndX=0 EndY=-1200.15 EndZ=0
    g3: LineSegment StartX=0 StartY=-1200.15 StartZ=0 EndX=0 EndY=-1219.2 EndZ=0
    g4: LineSegment StartX=0 StartY=0 StartZ=0 EndX=-22.225 EndY=0 EndZ=0
    g5: LineSegment StartX=-22.225 StartY=0 StartZ=0 EndX=-22.225 EndY=-19.05 EndZ=0
    g6: LineSegment StartX=-22.225 StartY=-19.05 StartZ=0 EndX=0 EndY=-19.05 EndZ=0
    g7: LineSegment StartX=0 StartY=-19.05 StartZ=0 EndX=0 EndY=0 EndZ=0
  constraints (22):
    c: Coincident(g0,g1)
    c: Coincident(g1,g2)
    c: Coincident(g2,g3)
    c: Coincident(g3,g0)
    c: Horizontal(g0)
    c: Horizontal(g2)
    c: Vertical(g1)
    c: Vertical(g3)
    c: Coincident(g0,g-4)
    c: PointOnObject(g1,g-3)
    c: DistanceY(g1,g1) = 19.05
    c: Coincident(g4,g5)
    c: Coincident(g5,g6)
    c: Coincident(g6,g7)
    c: Coincident(g7,g4)
    c: Horizontal(g4)
    c: Horizontal(g6)
    c: Vertical(g5)
    c: Vertical(g7)
    c: Coincident(g4,g-1)
    c: PointOnObject(g5,g-3)
    c: Distance(g5,g4) = 19.05
FEATURE [PartDesign::Pocket] Pocket002
  BaseFeature = -> Pad037
  Length = 5
  Length2 = 100
  Placement = pos=(0,0,0) rot=(1,0,0;1.5708rad)
  Profile = -> Sketch039
  Type = 1
FEATURE [PartDesign::Body] Body031  label="Al_L-Channel_1inx0p125inx48in_002"
  Group = -> [Sketch040,Pad037,Sketch039,Pocket002]
  Origin = -> Origin031
  Placement = pos=(-2501.56,1200.22,173.037) rot=(0,0,1;3.14159rad)
  Tip = -> Pocket002
FEATURE [Sketcher::SketchObject] Sketch042
  MapMode = 5
  Placement = pos=(0,0,0) rot=(1,0,0;1.5708rad)
  Support = -> [XZ_Plane032]
  sketch-geometry (6):
    g0: LineSegment StartX=25.4 StartY=25.4 StartZ=0 EndX=25.4 EndY=0 EndZ=0
    g1: LineSegment StartX=25.4 StartY=0 StartZ=0 EndX=0 EndY=0 EndZ=0
    g2: LineSegment StartX=0 StartY=0 StartZ=0 EndX=0 EndY=3.175 EndZ=0
    g3: LineSegment StartX=0 StartY=3.175 StartZ=0 EndX=22.225 EndY=3.175 EndZ=0
    g4: LineSegment StartX=22.225 StartY=3.175 StartZ=0 EndX=22.225 EndY=25.4 EndZ=0
    g5: LineSegment StartX=22.225 StartY=25.4 StartZ=0 EndX=25.4 EndY=25.4 EndZ=0
  constraints (17):
    c: PointOnObject(g0,g-1)
    c: Vertical(g0)
    c: Coincident(g0,g1)
    c: Coincident(g1,g-1)
    c: Coincident(g1,g2)
    c: PointOnObject(g2,g-2)
    c: Coincident(g2,g3)
    c: Horizontal(g3)
    c: Coincident(g3,g4)
    c: Vertical(g4)
    c: Coincident(g4,g5)
    c: Coincident(g5,g0)
    c: Equal(g5,g2)
    c: Equal(g3,g4)
    c: Equal(g0,g1)
    c: DistanceX(g1,g1) = 25.4
    c: DistanceX(g5,g5) = 3.175
FEATURE [PartDesign::Pad] Pad038
  Length = 1258.57
  Length2 = 100
  Placement = pos=(0,0,0) rot=(1,0,0;1.5708rad)
  Profile = -> Sketch042
  Reversed = true
  Type = 0
FEATURE [Sketcher::SketchObject] Sketch041
  ExternalGeometry = -> [Pad038]
  MapMode = 5
  Placement = pos=(0,0,3.175) rot=(0,0,1;3.14159rad)
  Support = -> [Pad038]
  sketch-geometry (8):
    g0: LineSegment StartX=0 StartY=-1258.57 StartZ=0 EndX=-22.225 EndY=-1258.57 EndZ=0
    g1: LineSegment StartX=-22.225 StartY=-1258.57 StartZ=0 EndX=-22.225 EndY=-1239.52 EndZ=0
    g2: LineSegment StartX=-22.225 StartY=-1239.52 StartZ=0 EndX=0 EndY=-1239.52 EndZ=0
    g3: LineSegment StartX=0 StartY=-1239.52 StartZ=0 EndX=0 EndY=-1258.57 EndZ=0
    g4: LineSegment StartX=0 StartY=0 StartZ=0 EndX=-22.225 EndY=0 EndZ=0
    g5: LineSegment StartX=-22.225 StartY=0 StartZ=0 EndX=-22.225 EndY=-19.05 EndZ=0
    g6: LineSegment StartX=-22.225 StartY=-19.05 StartZ=0 EndX=0 EndY=-19.05 EndZ=0
    g7: LineSegment StartX=0 StartY=-19.05 StartZ=0 EndX=0 EndY=0 EndZ=0
  constraints (22):
    c: Coincident(g0,g1)
    c: Coincident(g1,g2)
    c: Coincident(g2,g3)
    c: Coincident(g3,g0)
    c: Horizontal(g0)
    c: Horizontal(g2)
    c: Vertical(g1)
    c: Vertical(g3)
    c: Coincident(g0,g-4)
    c: PointOnObject(g1,g-3)
    c: DistanceY(g1,g1) = 19.05
    c: Coincident(g4,g5)
    c: Coincident(g5,g6)
    c: Coincident(g6,g7)
    c: Coincident(g7,g4)
    c: Horizontal(g4)
    c: Horizontal(g6)
    c: Vertical(g5)
    c: Vertical(g7)
    c: Coincident(g4,g-1)
    c: PointOnObject(g5,g-3)
    c: Distance(g5,g4) = 19.05
FEATURE [PartDesign::Pocket] Pocket003
  BaseFeature = -> Pad038
  Length = 5
  Length2 = 100
  Placement = pos=(0,0,0) rot=(1,0,0;1.5708rad)
  Profile = -> Sketch041
  Type = 1
FEATURE [PartDesign::Body] Body032  label="Al_L-Channel_1inx0p125inx49p55in_002"
  Group = -> [Sketch042,Pad038,Sketch041,Pocket003]
  Origin = -> Origin032
  Placement = pos=(-2501.56,2460.44,173.037) rot=(0,0,1;3.14159rad)
  Tip = -> Pocket003
FEATURE [Sketcher::SketchObject] Sketch044
  MapMode = 5
  Placement = pos=(0,0,0) rot=(1,0,0;1.5708rad)
  Support = -> [XZ_Plane033]
  sketch-geometry (6):
    g0: LineSegment StartX=25.4 StartY=25.4 StartZ=0 EndX=25.4 EndY=0 EndZ=0
    g1: LineSegment StartX=25.4 StartY=0 StartZ=0 EndX=0 EndY=0 EndZ=0
    g2: LineSegment StartX=0 StartY=0 StartZ=0 EndX=0 EndY=3.175 EndZ=0
    g3: LineSegment StartX=0 StartY=3.175 StartZ=0 EndX=22.225 EndY=3.175 EndZ=0
    g4: LineSegment StartX=22.225 StartY=3.175 StartZ=0 EndX=22.225 EndY=25.4 EndZ=0
    g5: LineSegment StartX=22.225 StartY=25.4 StartZ=0 EndX=25.4 EndY=25.4 EndZ=0
  constraints (17):
    c: PointOnObject(g0,g-1)
    c: Vertical(g0)
    c: Coincident(g0,g1)
    c: Coincident(g1,g-1)
    c: Coincident(g1,g2)
    c: PointOnObject(g2,g-2)
    c: Coincident(g2,g3)
    c: Horizontal(g3)
    c: Coincident(g3,g4)
    c: Vertical(g4)
    c: Coincident(g4,g5)
    c: Coincident(g5,g0)
    c: Equal(g5,g2)
    c: Equal(g3,g4)
    c: Equal(g0,g1)
    c: DistanceX(g1,g1) = 25.4
    c: DistanceX(g5,g5) = 3.175
FEATURE [PartDesign::Pad] Pad039
  Length = 1238.25
  Length2 = 100
  Placement = pos=(0,0,0) rot=(1,0,0;1.5708rad)
  Profile = -> Sketch044
  Reversed = true
  Type = 0
FEATURE [Sketcher::SketchObject] Sketch043
  ExternalGeometry = -> [Pad039]
  MapMode = 5
  Placement = pos=(0,7e-16,3.175) rot=(0,0,1;3.14159rad)
  Support = -> [Pad039]
  sketch-geometry (8):
    g0: LineSegment StartX=0 StartY=-1238.25 StartZ=0 EndX=-22.225 EndY=-1238.25 EndZ=0
    g1: LineSegment StartX=-22.225 StartY=-1238.25 StartZ=0 EndX=-22.225 EndY=-1219.2 EndZ=0
    g2: LineSegment StartX=-22.225 StartY=-1219.2 StartZ=0 EndX=0 EndY=-1219.2 EndZ=0
    g3: LineSegment StartX=0 StartY=-1219.2 StartZ=0 EndX=0 EndY=-1238.25 EndZ=0
    g4: LineSegment StartX=0 StartY=0 StartZ=0 EndX=-22.225 EndY=0 EndZ=0
    g5: LineSegment StartX=-22.225 StartY=0 StartZ=0 EndX=-22.225 EndY=-19.05 EndZ=0
    g6: LineSegment StartX=-22.225 StartY=-19.05 StartZ=0 EndX=0 EndY=-19.05 EndZ=0
    g7: LineSegment StartX=0 StartY=-19.05 StartZ=0 EndX=0 EndY=0 EndZ=0
  constraints (22):
    c: Coincident(g0,g1)
    c: Coincident(g1,g2)
    c: Coincident(g2,g3)
    c: Coincident(g3,g0)
    c: Horizontal(g0)
    c: Horizontal(g2)
    c: Vertical(g1)
    c: Vertical(g3)
    c: Coincident(g0,g-4)
    c: PointOnObject(g1,g-3)
    c: DistanceY(g1,g1) = 19.05
    c: Coincident(g4,g5)
    c: Coincident(g5,g6)
    c: Coincident(g6,g7)
    c: Coincident(g7,g4)
    c: Horizontal(g4)
    c: Horizontal(g6)
    c: Vertical(g5)
    c: Vertical(g7)
    c: Coincident(g4,g-1)
    c: PointOnObject(g5,g-3)
    c: Distance(g5,g4) = 19.05
FEATURE [PartDesign::Pocket] Pocket004
  BaseFeature = -> Pad039
  Length = 5
  Length2 = 100
  Placement = pos=(0,0,0) rot=(1,0,0;1.5708rad)
  Profile = -> Sketch043
  Type = 1
FEATURE [PartDesign::Body] Body033  label="Al_L-Channel_1inx0p125inx48p75in_001"
  Group = -> [Sketch044,Pad039,Sketch043,Pocket004]
  Origin = -> Origin033
  Placement = pos=(-22.1361,2457.77,173.037) rot=(0,0,1;1.5708rad)
  Tip = -> Pocket004
FEATURE [Sketcher::SketchObject] Sketch046
  MapMode = 5
  Placement = pos=(0,0,0) rot=(1,0,0;1.5708rad)
  Support = -> [XZ_Plane034]
  sketch-geometry (6):
    g0: LineSegment StartX=25.4 StartY=25.4 StartZ=0 EndX=25.4 EndY=0 EndZ=0
    g1: LineSegment StartX=25.4 StartY=0 StartZ=0 EndX=0 EndY=0 EndZ=0
    g2: LineSegment StartX=0 StartY=0 StartZ=0 EndX=0 EndY=3.175 EndZ=0
    g3: LineSegment StartX=0 StartY=3.175 StartZ=0 EndX=22.225 EndY=3.175 EndZ=0
    g4: LineSegment StartX=22.225 StartY=3.175 StartZ=0 EndX=22.225 EndY=25.4 EndZ=0
    g5: LineSegment StartX=22.225 StartY=25.4 StartZ=0 EndX=25.4 EndY=25.4 EndZ=0
  constraints (17):
    c: PointOnObject(g0,g-1)
    c: Vertical(g0)
    c: Coincident(g0,g1)
    c: Coincident(g1,g-1)
    c: Coincident(g1,g2)
    c: PointOnObject(g2,g-2)
    c: Coincident(g2,g3)
    c: Horizontal(g3)
    c: Coincident(g3,g4)
    c: Vertical(g4)
    c: Coincident(g4,g5)
    c: Coincident(g5,g0)
    c: Equal(g5,g2)
    c: Equal(g3,g4)
    c: Equal(g0,g1)
    c: DistanceX(g1,g1) = 25.4
    c: DistanceX(g5,g5) = 3.175
FEATURE [PartDesign::Pad] Pad040
  Length = 1238.25
  Length2 = 100
  Placement = pos=(0,0,0) rot=(1,0,0;1.5708rad)
  Profile = -> Sketch046
  Reversed = true
  Type = 0
FEATURE [Sketcher::SketchObject] Sketch045
  ExternalGeometry = -> [Pad040]
  MapMode = 5
  Placement = pos=(0,0,3.175) rot=(0,0,1;3.14159rad)
  Support = -> [Pad040]
  sketch-geometry (8):
    g0: LineSegment StartX=0 StartY=-1238.25 StartZ=0 EndX=-22.225 EndY=-1238.25 EndZ=0
    g1: LineSegment StartX=-22.225 StartY=-1238.25 StartZ=0 EndX=-22.225 EndY=-1219.2 EndZ=0
    g2: LineSegment StartX=-22.225 StartY=-1219.2 StartZ=0 EndX=0 EndY=-1219.2 EndZ=0
    g3: LineSegment StartX=0 StartY=-1219.2 StartZ=0 EndX=0 EndY=-1238.25 EndZ=0
    g4: LineSegment StartX=0 StartY=0 StartZ=0 EndX=-22.225 EndY=0 EndZ=0
    g5: LineSegment StartX=-22.225 StartY=0 StartZ=0 EndX=-22.225 EndY=-19.05 EndZ=0
    g6: LineSegment StartX=-22.225 StartY=-19.05 StartZ=0 EndX=0 EndY=-19.05 EndZ=0
    g7: LineSegment StartX=0 StartY=-19.05 StartZ=0 EndX=0 EndY=0 EndZ=0
  constraints (22):
    c: Coincident(g0,g1)
    c: Coincident(g1,g2)
    c: Coincident(g2,g3)
    c: Coincident(g3,g0)
    c: Horizontal(g0)
    c: Horizontal(g2)
    c: Vertical(g1)
    c: Vertical(g3)
    c: Coincident(g0,g-4)
    c: PointOnObject(g1,g-3)
    c: DistanceY(g1,g1) = 19.05
    c: Coincident(g4,g5)
    c: Coincident(g5,g6)
    c: Coincident(g6,g7)
    c: Coincident(g7,g4)
    c: Horizontal(g4)
    c: Horizontal(g6)
    c: Vertical(g5)
    c: Vertical(g7)
    c: Coincident(g4,g-1)
    c: PointOnObject(g5,g-3)
    c: Distance(g5,g4) = 19.05
FEATURE [PartDesign::Pocket] Pocket005
  BaseFeature = -> Pad040
  Length = 5
  Length2 = 100
  Placement = pos=(0,0,0) rot=(1,0,0;1.5708rad)
  Profile = -> Sketch045
  Type = 1
FEATURE [PartDesign::Body] Body034  label="Al_L-Channel_1inx0p125inx48p75in_002"
  Group = -> [Sketch046,Pad040,Sketch045,Pocket005]
  Origin = -> Origin034
  Placement = pos=(-1260.46,2457.77,173.037) rot=(0,0,1;1.5708rad)
  Tip = -> Pocket005
FEATURE [Sketcher::SketchObject] Sketch047
  MapMode = 5
  Placement = pos=(0,0,0) rot=(1,0,0;1.5708rad)
  Support = -> [XZ_Plane035]
  sketch-geometry (6):
    g0: LineSegment StartX=25.4 StartY=25.4 StartZ=0 EndX=25.4 EndY=0 EndZ=0
    g1: LineSegment StartX=25.4 StartY=0 StartZ=0 EndX=0 EndY=0 EndZ=0
    g2: LineSegment StartX=0 StartY=0 StartZ=0 EndX=0 EndY=3.175 EndZ=0
    g3: LineSegment StartX=0 StartY=3.175 StartZ=0 EndX=22.225 EndY=3.175 EndZ=0
    g4: LineSegment StartX=22.225 StartY=3.175 StartZ=0 EndX=22.225 EndY=25.4 EndZ=0
    g5: LineSegment StartX=22.225 StartY=25.4 StartZ=0 EndX=25.4 EndY=25.4 EndZ=0
  constraints (17):
    c: PointOnObject(g0,g-1)
    c: Vertical(g0)
    c: Coincident(g0,g1)
    c: Coincident(g1,g-1)
    c: Coincident(g1,g2)
    c: PointOnObject(g2,g-2)
    c: Coincident(g2,g3)
    c: Horizontal(g3)
    c: Coincident(g3,g4)
    c: Vertical(g4)
    c: Coincident(g4,g5)
    c: Coincident(g5,g0)
    c: Equal(g5,g2)
    c: Equal(g3,g4)
    c: Equal(g0,g1)
    c: DistanceX(g1,g1) = 25.4
    c: DistanceX(g5,g5) = 3.175
FEATURE [PartDesign::Pad] Pad041
  Length = 1252.22
  Length2 = 100
  Placement = pos=(0,0,0) rot=(1,0,0;1.5708rad)
  Profile = -> Sketch047
  Reversed = true
  Type = 0
FEATURE [Sketcher::SketchObject] Sketch048
  ExternalGeometry = -> [Pad041]
  MapMode = 5
  Placement = pos=(0,7e-16,3.175) rot=(0,0,1;3.14159rad)
  Support = -> [Pad041]
  sketch-geometry (8):
    g0: LineSegment StartX=0 StartY=-1252.22 StartZ=0 EndX=-22.225 EndY=-1252.22 EndZ=0
    g1: LineSegment StartX=-22.225 StartY=-1252.22 StartZ=0 EndX=-22.225 EndY=-1233.17 EndZ=0
    g2: LineSegment StartX=-22.225 StartY=-1233.17 StartZ=0 EndX=0 EndY=-1233.17 EndZ=0
    g3: LineSegment StartX=0 StartY=-1233.17 StartZ=0 EndX=0 EndY=-1252.22 EndZ=0
    g4: LineSegment StartX=0 StartY=0 StartZ=0 EndX=-22.225 EndY=0 EndZ=0
    g5: LineSegment StartX=-22.225 StartY=0 StartZ=0 EndX=-22.225 EndY=-19.05 EndZ=0
    g6: LineSegment StartX=-22.225 StartY=-19.05 StartZ=0 EndX=0 EndY=-19.05 EndZ=0
    g7: LineSegment StartX=0 StartY=-19.05 StartZ=0 EndX=0 EndY=0 EndZ=0
  constraints (22):
    c: Coincident(g0,g1)
    c: Coincident(g1,g2)
    c: Coincident(g2,g3)
    c: Coincident(g3,g0)
    c: Horizontal(g0)
    c: Horizontal(g2)
    c: Vertical(g1)
    c: Vertical(g3)
    c: Coincident(g0,g-4)
    c: PointOnObject(g1,g-3)
    c: DistanceY(g1,g1) = 19.05
    c: Coincident(g4,g5)
    c: Coincident(g5,g6)
    c: Coincident(g6,g7)
    c: Coincident(g7,g4)
    c: Horizontal(g4)
    c: Horizontal(g6)
    c: Vertical(g5)
    c: Vertical(g7)
    c: Coincident(g4,g-1)
    c: PointOnObject(g5,g-3)
    c: Distance(g5,g4) = 19.05
FEATURE [PartDesign::Pocket] Pocket006
  BaseFeature = -> Pad041
  Length = 5
  Length2 = 100
  Placement = pos=(0,0,0) rot=(1,0,0;1.5708rad)
  Profile = -> Sketch048
  Type = 1
FEATURE [PartDesign::Body] Body035  label="Al_L-Channel_1inx0p125inx49p3in_001"
  Group = -> [Sketch047,Pad041,Sketch048,Pocket006]
  Origin = -> Origin035
  Placement = pos=(-1888.81,-29.0173,173.037) rot=(0,0,1;3.14159rad)
  Tip = -> Pocket006
FEATURE [Sketcher::SketchObject] Sketch050
  MapMode = 5
  Placement = pos=(0,0,0) rot=(1,0,0;1.5708rad)
  Support = -> [XZ_Plane036]
  sketch-geometry (6):
    g0: LineSegment StartX=25.4 StartY=25.4 StartZ=0 EndX=25.4 EndY=0 EndZ=0
    g1: LineSegment StartX=25.4 StartY=0 StartZ=0 EndX=0 EndY=0 EndZ=0
    g2: LineSegment StartX=0 StartY=0 StartZ=0 EndX=0 EndY=3.175 EndZ=0
    g3: LineSegment StartX=0 StartY=3.175 StartZ=0 EndX=22.225 EndY=3.175 EndZ=0
    g4: LineSegment StartX=22.225 StartY=3.175 StartZ=0 EndX=22.225 EndY=25.4 EndZ=0
    g5: LineSegment StartX=22.225 StartY=25.4 StartZ=0 EndX=25.4 EndY=25.4 EndZ=0
  constraints (17):
    c: PointOnObject(g0,g-1)
    c: Vertical(g0)
    c: Coincident(g0,g1)
    c: Coincident(g1,g-1)
    c: Coincident(g1,g2)
    c: PointOnObject(g2,g-2)
    c: Coincident(g2,g3)
    c: Horizontal(g3)
    c: Coincident(g3,g4)
    c: Vertical(g4)
    c: Coincident(g4,g5)
    c: Coincident(g5,g0)
    c: Equal(g5,g2)
    c: Equal(g3,g4)
    c: Equal(g0,g1)
    c: DistanceX(g1,g1) = 25.4
    c: DistanceX(g5,g5) = 3.175
FEATURE [PartDesign::Pad] Pad042
  Length = 1252.22
  Length2 = 100
  Placement = pos=(0,0,0) rot=(1,0,0;1.5708rad)
  Profile = -> Sketch050
  Reversed = true
  Type = 0
FEATURE [Sketcher::SketchObject] Sketch049
  ExternalGeometry = -> [Pad042]
  MapMode = 5
  Placement = pos=(0,0,3.175) rot=(0,0,1;3.14159rad)
  Support = -> [Pad042]
  sketch-geometry (8):
    g0: LineSegment StartX=0 StartY=-1252.22 StartZ=0 EndX=-22.225 EndY=-1252.22 EndZ=0
    g1: LineSegment StartX=-22.225 StartY=-1252.22 StartZ=0 EndX=-22.225 EndY=-1233.17 EndZ=0
    g2: LineSegment StartX=-22.225 StartY=-1233.17 StartZ=0 EndX=0 EndY=-1233.17 EndZ=0
    g3: LineSegment StartX=0 StartY=-1233.17 StartZ=0 EndX=0 EndY=-1252.22 EndZ=0
    g4: LineSegment StartX=0 StartY=0 StartZ=0 EndX=-22.225 EndY=0 EndZ=0
    g5: LineSegment StartX=-22.225 StartY=0 StartZ=0 EndX=-22.225 EndY=-19.05 EndZ=0
    g6: LineSegment StartX=-22.225 StartY=-19.05 StartZ=0 EndX=0 EndY=-19.05 EndZ=0
    g7: LineSegment StartX=0 StartY=-19.05 StartZ=0 EndX=0 EndY=0 EndZ=0
  constraints (22):
    c: Coincident(g0,g1)
    c: Coincident(g1,g2)
    c: Coincident(g2,g3)
    c: Coincident(g3,g0)
    c: Horizontal(g0)
    c: Horizontal(g2)
    c: Vertical(g1)
    c: Vertical(g3)
    c: Coincident(g0,g-4)
    c: PointOnObject(g1,g-3)
    c: DistanceY(g1,g1) = 19.05
    c: Coincident(g4,g5)
    c: Coincident(g5,g6)
    c: Coincident(g6,g7)
    c: Coincident(g7,g4)
    c: Horizontal(g4)
    c: Horizontal(g6)
    c: Vertical(g5)
    c: Vertical(g7)
    c: Coincident(g4,g-1)
    c: PointOnObject(g5,g-3)
    c: Distance(g5,g4) = 19.05
FEATURE [PartDesign::Pocket] Pocket007
  BaseFeature = -> Pad042
  Length = 5
  Length2 = 100
  Placement = pos=(0,0,0) rot=(1,0,0;1.5708rad)
  Profile = -> Sketch049
  Type = 1
FEATURE [PartDesign::Body] Body036  label="Al_L-Channel_1inx0p125inx49p3in_002"
  Group = -> [Sketch050,Pad042,Sketch049,Pocket007]
  Origin = -> Origin036
  Placement = pos=(-628.585,-1281.24,173.037) rot=(0,0,1;0rad)
  Tip = -> Pocket007
FEATURE [Sketcher::SketchObject] Sketch051
  MapMode = 5
  Placement = pos=(0,0,0) rot=(1,0,0;1.5708rad)
  Support = -> [XZ_Plane037]
  sketch-geometry (6):
    g0: LineSegment StartX=25.4 StartY=25.4 StartZ=0 EndX=25.4 EndY=0 EndZ=0
    g1: LineSegment StartX=25.4 StartY=0 StartZ=0 EndX=0 EndY=0 EndZ=0
    g2: LineSegment StartX=0 StartY=0 StartZ=0 EndX=0 EndY=3.175 EndZ=0
    g3: LineSegment StartX=0 StartY=3.175 StartZ=0 EndX=22.225 EndY=3.175 EndZ=0
    g4: LineSegment StartX=22.225 StartY=3.175 StartZ=0 EndX=22.225 EndY=25.4 EndZ=0
    g5: LineSegment StartX=22.225 StartY=25.4 StartZ=0 EndX=25.4 EndY=25.4 EndZ=0
  constraints (17):
    c: PointOnObject(g0,g-1)
    c: Vertical(g0)
    c: Coincident(g0,g1)
    c: Coincident(g1,g-1)
    c: Coincident(g1,g2)
    c: PointOnObject(g2,g-2)
    c: Coincident(g2,g3)
    c: Horizontal(g3)
    c: Coincident(g3,g4)
    c: Vertical(g4)
    c: Coincident(g4,g5)
    c: Coincident(g5,g0)
    c: Equal(g5,g2)
    c: Equal(g3,g4)
    c: Equal(g0,g1)
    c: DistanceX(g1,g1) = 25.4
    c: DistanceX(g5,g5) = 3.175
FEATURE [PartDesign::Pad] Pad043
  Length = 609.6
  Length2 = 100
  Placement = pos=(0,0,0) rot=(1,0,0;1.5708rad)
  Profile = -> Sketch051
  Reversed = true
  Type = 0
FEATURE [Sketcher::SketchObject] Sketch052
  ExternalGeometry = -> [Pad043]
  MapMode = 5
  Placement = pos=(0,7e-16,3.175) rot=(0,0,1;3.14159rad)
  Support = -> [Pad043]
  sketch-geometry (8):
    g0: LineSegment StartX=0 StartY=-609.6 StartZ=0 EndX=-22.225 EndY=-609.6 EndZ=0
    g1: LineSegment StartX=-22.225 StartY=-609.6 StartZ=0 EndX=-22.225 EndY=-590.55 EndZ=0
    g2: LineSegment StartX=-22.225 StartY=-590.55 StartZ=0 EndX=0 EndY=-590.55 EndZ=0
    g3: LineSegment StartX=0 StartY=-590.55 StartZ=0 EndX=0 EndY=-609.6 EndZ=0
    g4: LineSegment StartX=0 StartY=0 StartZ=0 EndX=-22.225 EndY=0 EndZ=0
    g5: LineSegment StartX=-22.225 StartY=0 StartZ=0 EndX=-22.225 EndY=-19.05 EndZ=0
    g6: LineSegment StartX=-22.225 StartY=-19.05 StartZ=0 EndX=0 EndY=-19.05 EndZ=0
    g7: LineSegment StartX=0 StartY=-19.05 StartZ=0 EndX=0 EndY=0 EndZ=0
  constraints (22):
    c: Coincident(g0,g1)
    c: Coincident(g1,g2)
    c: Coincident(g2,g3)
    c: Coincident(g3,g0)
    c: Horizontal(g0)
    c: Horizontal(g2)
    c: Vertical(g1)
    c: Vertical(g3)
    c: Coincident(g0,g-4)
    c: PointOnObject(g1,g-3)
    c: DistanceY(g1,g1) = 19.05
    c: Coincident(g4,g5)
    c: Coincident(g5,g6)
    c: Coincident(g6,g7)
    c: Coincident(g7,g4)
    c: Horizontal(g4)
    c: Horizontal(g6)
    c: Vertical(g5)
    c: Vertical(g7)
    c: Coincident(g4,g-1)
    c: PointOnObject(g5,g-3)
    c: Distance(g5,g4) = 19.05
FEATURE [PartDesign::Pocket] Pocket008
  BaseFeature = -> Pad043
  Length = 5
  Length2 = 100
  Placement = pos=(0,0,0) rot=(1,0,0;1.5708rad)
  Profile = -> Sketch052
  Type = 1
FEATURE [PartDesign::Body] Body037  label="Al_L-Channel_1inx0p125inx24in_001"
  Group = -> [Sketch051,Pad043,Sketch052,Pocket008]
  Origin = -> Origin037
  Placement = pos=(-628.585,-21.0163,173.037) rot=(0,0,-1;1.5708rad)
  Tip = -> Pocket008
FEATURE [Sketcher::SketchObject] Sketch053
  MapMode = 5
  Placement = pos=(0,0,0) rot=(1,0,0;1.5708rad)
  Support = -> [XZ_Plane038]
  sketch-geometry (6):
    g0: LineSegment StartX=25.4 StartY=25.4 StartZ=0 EndX=25.4 EndY=0 EndZ=0
    g1: LineSegment StartX=25.4 StartY=0 StartZ=0 EndX=0 EndY=0 EndZ=0
    g2: LineSegment StartX=0 StartY=0 StartZ=0 EndX=0 EndY=3.175 EndZ=0
    g3: LineSegment StartX=0 StartY=3.175 StartZ=0 EndX=22.225 EndY=3.175 EndZ=0
    g4: LineSegment StartX=22.225 StartY=3.175 StartZ=0 EndX=22.225 EndY=25.4 EndZ=0
    g5: LineSegment StartX=22.225 StartY=25.4 StartZ=0 EndX=25.4 EndY=25.4 EndZ=0
  constraints (17):
    c: PointOnObject(g0,g-1)
    c: Vertical(g0)
    c: Coincident(g0,g1)
    c: Coincident(g1,g-1)
    c: Coincident(g1,g2)
    c: PointOnObject(g2,g-2)
    c: Coincident(g2,g3)
    c: Horizontal(g3)
    c: Coincident(g3,g4)
    c: Vertical(g4)
    c: Coincident(g4,g5)
    c: Coincident(g5,g0)
    c: Equal(g5,g2)
    c: Equal(g3,g4)
    c: Equal(g0,g1)
    c: DistanceX(g1,g1) = 25.4
    c: DistanceX(g5,g5) = 3.175
FEATURE [PartDesign::Pad] Pad044
  Length = 609.6
  Length2 = 100
  Placement = pos=(0,0,0) rot=(1,0,0;1.5708rad)
  Profile = -> Sketch053
  Reversed = true
  Type = 0
FEATURE [Sketcher::SketchObject] Sketch054
  ExternalGeometry = -> [Pad044]
  MapMode = 5
  Placement = pos=(0,0,3.175) rot=(0,0,1;3.14159rad)
  Support = -> [Pad044]
  sketch-geometry (8):
    g0: LineSegment StartX=0 StartY=-609.6 StartZ=0 EndX=-22.225 EndY=-609.6 EndZ=0
    g1: LineSegment StartX=-22.225 StartY=-609.6 StartZ=0 EndX=-22.225 EndY=-590.55 EndZ=0
    g2: LineSegment StartX=-22.225 StartY=-590.55 StartZ=0 EndX=0 EndY=-590.55 EndZ=0
    g3: LineSegment StartX=0 StartY=-590.55 StartZ=0 EndX=0 EndY=-609.6 EndZ=0
    g4: LineSegment StartX=0 StartY=0 StartZ=0 EndX=-22.225 EndY=0 EndZ=0
    g5: LineSegment StartX=-22.225 StartY=0 StartZ=0 EndX=-22.225 EndY=-19.05 EndZ=0
    g6: LineSegment StartX=-22.225 StartY=-19.05 StartZ=0 EndX=0 EndY=-19.05 EndZ=0
    g7: LineSegment StartX=0 StartY=-19.05 StartZ=0 EndX=0 EndY=0 EndZ=0
  constraints (22):
    c: Coincident(g0,g1)
    c: Coincident(g1,g2)
    c: Coincident(g2,g3)
    c: Coincident(g3,g0)
    c: Horizontal(g0)
    c: Horizontal(g2)
    c: Vertical(g1)
    c: Vertical(g3)
    c: Coincident(g0,g-4)
    c: PointOnObject(g1,g-3)
    c: DistanceY(g1,g1) = 19.05
    c: Coincident(g4,g5)
    c: Coincident(g5,g6)
    c: Coincident(g6,g7)
    c: Coincident(g7,g4)
    c: Horizontal(g4)
    c: Horizontal(g6)
    c: Vertical(g5)
    c: Vertical(g7)
    c: Coincident(g4,g-1)
    c: PointOnObject(g5,g-3)
    c: Distance(g5,g4) = 19.05
FEATURE [PartDesign::Pocket] Pocket009
  BaseFeature = -> Pad044
  Length = 5
  Length2 = 100
  Placement = pos=(0,0,0) rot=(1,0,0;1.5708rad)
  Profile = -> Sketch054
  Type = 1
FEATURE [PartDesign::Body] Body038  label="Al_L-Channel_1inx0p125inx24in_002"
  Group = -> [Sketch053,Pad044,Sketch054,Pocket009]
  Origin = -> Origin038
  Placement = pos=(-2500.17,-21.0163,173.037) rot=(0,0,-1;1.5708rad)
  Tip = -> Pocket009
FEATURE [Sketcher::SketchObject] Sketch055
  MapMode = 5
  Placement = pos=(0,0,0) rot=(1,0,0;1.5708rad)
  Support = -> [XZ_Plane039]
  sketch-geometry (4):
    g0: LineSegment StartX=41.021 StartY=41.021 StartZ=0 EndX=0 EndY=41.021 EndZ=0
    g1: LineSegment StartX=0 StartY=41.021 StartZ=0 EndX=0 EndY=0 EndZ=0
    g2: LineSegment StartX=0 StartY=0 StartZ=0 EndX=41.021 EndY=0 EndZ=0
    g3: LineSegment StartX=41.021 StartY=0 StartZ=0 EndX=41.021 EndY=41.021 EndZ=0
  constraints (11):
    c: Coincident(g0,g1)
    c: Coincident(g1,g2)
    c: Coincident(g2,g3)
    c: Coincident(g3,g0)
    c: Horizontal(g0)
    c: Horizontal(g2)
    c: Vertical(g1)
    c: Vertical(g3)
    c: Coincident(g1,g-1)
    c: Equal(g0,g3)
    c: DistanceX(g0,g0) = 41.021
FEATURE [PartDesign::Pad] Pad045
  Length = 41.021
  Length2 = 100
  Placement = pos=(0,0,0) rot=(1,0,0;1.5708rad)
  Profile = -> Sketch055
  Type = 0
FEATURE [Sketcher::SketchObject] Sketch056
  MapMode = 5
  Placement = pos=(0,0,0) rot=(1,0,0;3.14159rad)
  Support = -> [Pad045]
  sketch-geometry (7):
    g0: LineSegment StartX=7.5534 StartY=33.4614 StartZ=0 EndX=33.4614 EndY=33.4614 EndZ=0
    g1: LineSegment StartX=33.4614 StartY=33.4614 StartZ=0 EndX=33.4614 EndY=7.5534 EndZ=0
    g2: LineSegment StartX=33.4614 StartY=7.5534 StartZ=0 EndX=7.5534 EndY=7.5534 EndZ=0
    g3: LineSegment StartX=7.5534 StartY=7.5534 StartZ=0 EndX=7.5534 EndY=33.4614 EndZ=0
    g4: LineSegment [constr] StartX=0 StartY=0 StartZ=0 EndX=7.5534 EndY=7.5534 EndZ=0
    g5: LineSegment [constr] StartX=20.5074 StartY=20.5074 StartZ=0 EndX=7.5534 EndY=7.5534 EndZ=0
    g6: LineSegment [constr] StartX=20.5074 StartY=20.5074 StartZ=0 EndX=33.4614 EndY=33.4614 EndZ=0
  constraints (19):
    c: Coincident(g0,g1)
    c: Coincident(g1,g2)
    c: Coincident(g2,g3)
    c: Coincident(g3,g0)
    c: Horizontal(g0)
    c: Horizontal(g2)
    c: Vertical(g1)
    c: Vertical(g3)
    c: Equal(g2,g3)
    c: Coincident(g4,g-1)
    c: Coincident(g4,g2)
    c: Coincident(g5,g2)
    c: Parallel(g5,g4)
    c: Distance(g-1,g5) = 29.0018
    c: Angle(g-1,g4) = 0.785398
    c: Coincident(g6,g5)
    c: Coincident(g6,g0)
    c: Equal(g6,g5)
    c: DistanceX(g0,g0) = 25.908
FEATURE [PartDesign::Pad] Pad046
  BaseFeature = -> Pad045
  Length = 6.35
  Length2 = 100
  Placement = pos=(0,0,0) rot=(1,0,0;1.5708rad)
  Profile = -> Sketch056
  Type = 0
FEATURE [PartDesign::Fillet] Fillet
  Base = -> Pad046 [Edge24,Edge19,Edge23,Edge21]
  BaseFeature = -> Pad046
  Placement = pos=(0,0,0) rot=(1,0,0;1.5708rad)
  Radius = 3.556
FEATURE [PartDesign::Fillet] Fillet001
  Base = -> Fillet [Edge30,Edge31,Edge32]
  BaseFeature = -> Fillet
  Placement = pos=(0,0,0) rot=(1,0,0;1.5708rad)
  Radius = 3.556
FEATURE [PartDesign::Body] Body039  label="1p615in_Corner_Smoothed_001"
  Group = -> [Sketch055,Pad045,Sketch056,Pad046,Fillet,Fillet001]
  Origin = -> Origin039
  Placement = pos=(-41.1226,-0.0508,2459.18) rot=(0,0,1;0rad)
  Tip = -> Fillet001
FEATURE [Sketcher::SketchObject] Sketch058
  MapMode = 5
  Placement = pos=(0,0,0) rot=(1,0,0;1.5708rad)
  Support = -> [XZ_Plane040]
  sketch-geometry (4):
    g0: LineSegment StartX=41.021 StartY=41.021 StartZ=0 EndX=0 EndY=41.021 EndZ=0
    g1: LineSegment StartX=0 StartY=41.021 StartZ=0 EndX=0 EndY=0 EndZ=0
    g2: LineSegment StartX=0 StartY=0 StartZ=0 EndX=41.021 EndY=0 EndZ=0
    g3: LineSegment StartX=41.021 StartY=0 StartZ=0 EndX=41.021 EndY=41.021 EndZ=0
  constraints (11):
    c: Coincident(g0,g1)
    c: Coincident(g1,g2)
    c: Coincident(g2,g3)
    c: Coincident(g3,g0)
    c: Horizontal(g0)
    c: Horizontal(g2)
    c: Vertical(g1)
    c: Vertical(g3)
    c: Coincident(g1,g-1)
    c: Equal(g0,g3)
    c: DistanceX(g0,g0) = 41.021
FEATURE [PartDesign::Pad] Pad047
  Length = 41.021
  Length2 = 100
  Placement = pos=(0,0,0) rot=(1,0,0;1.5708rad)
  Profile = -> Sketch058
  Type = 0
FEATURE [Sketcher::SketchObject] Sketch057
  MapMode = 5
  Placement = pos=(0,0,0) rot=(1,0,0;3.14159rad)
  Support = -> [Pad047]
  sketch-geometry (7):
    g0: LineSegment StartX=7.5534 StartY=33.4614 StartZ=0 EndX=33.4614 EndY=33.4614 EndZ=0
    g1: LineSegment StartX=33.4614 StartY=33.4614 StartZ=0 EndX=33.4614 EndY=7.5534 EndZ=0
    g2: LineSegment StartX=33.4614 StartY=7.5534 StartZ=0 EndX=7.5534 EndY=7.5534 EndZ=0
    g3: LineSegment StartX=7.5534 StartY=7.5534 StartZ=0 EndX=7.5534 EndY=33.4614 EndZ=0
    g4: LineSegment [constr] StartX=0 StartY=0 StartZ=0 EndX=7.5534 EndY=7.5534 EndZ=0
    g5: LineSegment [constr] StartX=20.5074 StartY=20.5074 StartZ=0 EndX=7.5534 EndY=7.5534 EndZ=0
    g6: LineSegment [constr] StartX=20.5074 StartY=20.5074 StartZ=0 EndX=33.4614 EndY=33.4614 EndZ=0
  constraints (19):
    c: Coincident(g0,g1)
    c: Coincident(g1,g2)
    c: Coincident(g2,g3)
    c: Coincident(g3,g0)
    c: Horizontal(g0)
    c: Horizontal(g2)
    c: Vertical(g1)
    c: Vertical(g3)
    c: Equal(g2,g3)
    c: Coincident(g4,g-1)
    c: Coincident(g4,g2)
    c: Coincident(g5,g2)
    c: Parallel(g5,g4)
    c: Distance(g-1,g5) = 29.0018
    c: Angle(g-1,g4) = 0.785398
    c: Coincident(g6,g5)
    c: Coincident(g6,g0)
    c: Equal(g6,g5)
    c: DistanceX(g0,g0) = 25.908
FEATURE [PartDesign::Pad] Pad048
  BaseFeature = -> Pad047
  Length = 6.35
  Length2 = 100
  Placement = pos=(0,0,0) rot=(1,0,0;1.5708rad)
  Profile = -> Sketch057
  Type = 0
FEATURE [PartDesign::Fillet] Fillet002
  Base = -> Pad048 [Edge24,Edge19,Edge23,Edge21]
  BaseFeature = -> Pad048
  Placement = pos=(0,0,0) rot=(1,0,0;1.5708rad)
  Radius = 3.556
FEATURE [PartDesign::Fillet] Fillet003
  Base = -> Fillet002 [Edge30,Edge31,Edge32]
  BaseFeature = -> Fillet002
  Placement = pos=(0,0,0) rot=(1,0,0;1.5708rad)
  Radius = 3.556
FEATURE [PartDesign::Body] Body040  label="1p615in_Corner_Smoothed_002"
  Group = -> [Sketch058,Pad047,Sketch057,Pad048,Fillet002,Fillet003]
  Origin = -> Origin040
  Placement = pos=(-650.669,-1260.81,2459.18) rot=(0,0,1;0rad)
  Tip = -> Fillet003
FEATURE [Sketcher::SketchObject] Sketch060
  MapMode = 5
  Placement = pos=(0,0,0) rot=(1,0,0;1.5708rad)
  Support = -> [XZ_Plane041]
  sketch-geometry (4):
    g0: LineSegment StartX=41.021 StartY=41.021 StartZ=0 EndX=0 EndY=41.021 EndZ=0
    g1: LineSegment StartX=0 StartY=41.021 StartZ=0 EndX=0 EndY=0 EndZ=0
    g2: LineSegment StartX=0 StartY=0 StartZ=0 EndX=41.021 EndY=0 EndZ=0
    g3: LineSegment StartX=41.021 StartY=0 StartZ=0 EndX=41.021 EndY=41.021 EndZ=0
  constraints (11):
    c: Coincident(g0,g1)
    c: Coincident(g1,g2)
    c: Coincident(g2,g3)
    c: Coincident(g3,g0)
    c: Horizontal(g0)
    c: Horizontal(g2)
    c: Vertical(g1)
    c: Vertical(g3)
    c: Coincident(g1,g-1)
    c: Equal(g0,g3)
    c: DistanceX(g0,g0) = 41.021
FEATURE [PartDesign::Pad] Pad050
  Length = 41.021
  Length2 = 100
  Placement = pos=(0,0,0) rot=(1,0,0;1.5708rad)
  Profile = -> Sketch060
  Type = 0
FEATURE [Sketcher::SketchObject] Sketch059
  MapMode = 5
  Placement = pos=(0,0,0) rot=(1,0,0;3.14159rad)
  Support = -> [Pad050]
  sketch-geometry (7):
    g0: LineSegment StartX=7.5534 StartY=33.4614 StartZ=0 EndX=33.4614 EndY=33.4614 EndZ=0
    g1: LineSegment StartX=33.4614 StartY=33.4614 StartZ=0 EndX=33.4614 EndY=7.5534 EndZ=0
    g2: LineSegment StartX=33.4614 StartY=7.5534 StartZ=0 EndX=7.5534 EndY=7.5534 EndZ=0
    g3: LineSegment StartX=7.5534 StartY=7.5534 StartZ=0 EndX=7.5534 EndY=33.4614 EndZ=0
    g4: LineSegment [constr] StartX=0 StartY=0 StartZ=0 EndX=7.5534 EndY=7.5534 EndZ=0
    g5: LineSegment [constr] StartX=20.5074 StartY=20.5074 StartZ=0 EndX=7.5534 EndY=7.5534 EndZ=0
    g6: LineSegment [constr] StartX=20.5074 StartY=20.5074 StartZ=0 EndX=33.4614 EndY=33.4614 EndZ=0
  constraints (19):
    c: Coincident(g0,g1)
    c: Coincident(g1,g2)
    c: Coincident(g2,g3)
    c: Coincident(g3,g0)
    c: Horizontal(g0)
    c: Horizontal(g2)
    c: Vertical(g1)
    c: Vertical(g3)
    c: Equal(g2,g3)
    c: Coincident(g4,g-1)
    c: Coincident(g4,g2)
    c: Coincident(g5,g2)
    c: Parallel(g5,g4)
    c: Distance(g-1,g5) = 29.0018
    c: Angle(g-1,g4) = 0.785398
    c: Coincident(g6,g5)
    c: Coincident(g6,g0)
    c: Equal(g6,g5)
    c: DistanceX(g0,g0) = 25.908
FEATURE [PartDesign::Pad] Pad049
  BaseFeature = -> Pad050
  Length = 6.35
  Length2 = 100
  Placement = pos=(0,0,0) rot=(1,0,0;1.5708rad)
  Profile = -> Sketch059
  Type = 0
FEATURE [PartDesign::Fillet] Fillet005
  Base = -> Pad049 [Edge24,Edge19,Edge23,Edge21]
  BaseFeature = -> Pad049
  Placement = pos=(0,0,0) rot=(1,0,0;1.5708rad)
  Radius = 3.556
FEATURE [PartDesign::Fillet] Fillet004
  Base = -> Fillet005 [Edge30,Edge31,Edge32]
  BaseFeature = -> Fillet005
  Placement = pos=(0,0,0) rot=(1,0,0;1.5708rad)
  Radius = 3.556
FEATURE [PartDesign::Body] Body041  label="1p615in_Corner_Smoothed_003"
  Group = -> [Sketch060,Pad050,Sketch059,Pad049,Fillet005,Fillet004]
  Origin = -> Origin041
  Placement = pos=(-1870.4,-1260.81,2459.18) rot=(0,0,1;4.71239rad)
  Tip = -> Fillet004
FEATURE [Sketcher::SketchObject] Sketch062
  MapMode = 5
  Placement = pos=(0,0,0) rot=(1,0,0;1.5708rad)
  Support = -> [XZ_Plane042]
  sketch-geometry (4):
    g0: LineSegment StartX=41.021 StartY=41.021 StartZ=0 EndX=0 EndY=41.021 EndZ=0
    g1: LineSegment StartX=0 StartY=41.021 StartZ=0 EndX=0 EndY=0 EndZ=0
    g2: LineSegment StartX=0 StartY=0 StartZ=0 EndX=41.021 EndY=0 EndZ=0
    g3: LineSegment StartX=41.021 StartY=0 StartZ=0 EndX=41.021 EndY=41.021 EndZ=0
  constraints (11):
    c: Coincident(g0,g1)
    c: Coincident(g1,g2)
    c: Coincident(g2,g3)
    c: Coincident(g3,g0)
    c: Horizontal(g0)
    c: Horizontal(g2)
    c: Vertical(g1)
    c: Vertical(g3)
    c: Coincident(g1,g-1)
    c: Equal(g0,g3)
    c: DistanceX(g0,g0) = 41.021
FEATURE [PartDesign::Pad] Pad052
  Length = 41.021
  Length2 = 100
  Placement = pos=(0,0,0) rot=(1,0,0;1.5708rad)
  Profile = -> Sketch062
  Type = 0
FEATURE [Sketcher::SketchObject] Sketch061
  MapMode = 5
  Placement = pos=(0,0,0) rot=(1,0,0;3.14159rad)
  Support = -> [Pad052]
  sketch-geometry (7):
    g0: LineSegment StartX=7.5534 StartY=33.4614 StartZ=0 EndX=33.4614 EndY=33.4614 EndZ=0
    g1: LineSegment StartX=33.4614 StartY=33.4614 StartZ=0 EndX=33.4614 EndY=7.5534 EndZ=0
    g2: LineSegment StartX=33.4614 StartY=7.5534 StartZ=0 EndX=7.5534 EndY=7.5534 EndZ=0
    g3: LineSegment StartX=7.5534 StartY=7.5534 StartZ=0 EndX=7.5534 EndY=33.4614 EndZ=0
    g4: LineSegment [constr] StartX=0 StartY=0 StartZ=0 EndX=7.5534 EndY=7.5534 EndZ=0
    g5: LineSegment [constr] StartX=20.5074 StartY=20.5074 StartZ=0 EndX=7.5534 EndY=7.5534 EndZ=0
    g6: LineSegment [constr] StartX=20.5074 StartY=20.5074 StartZ=0 EndX=33.4614 EndY=33.4614 EndZ=0
  constraints (19):
    c: Coincident(g0,g1)
    c: Coincident(g1,g2)
    c: Coincident(g2,g3)
    c: Coincident(g3,g0)
    c: Horizontal(g0)
    c: Horizontal(g2)
    c: Vertical(g1)
    c: Vertical(g3)
    c: Equal(g2,g3)
    c: Coincident(g4,g-1)
    c: Coincident(g4,g2)
    c: Coincident(g5,g2)
    c: Parallel(g5,g4)
    c: Distance(g-1,g5) = 29.0018
    c: Angle(g-1,g4) = 0.785398
    c: Coincident(g6,g5)
    c: Coincident(g6,g0)
    c: Equal(g6,g5)
    c: DistanceX(g0,g0) = 25.908
FEATURE [PartDesign::Pad] Pad051
  BaseFeature = -> Pad052
  Length = 6.35
  Length2 = 100
  Placement = pos=(0,0,0) rot=(1,0,0;1.5708rad)
  Profile = -> Sketch061
  Type = 0
FEATURE [PartDesign::Fillet] Fillet006
  Base = -> Pad051 [Edge24,Edge19,Edge23,Edge21]
  BaseFeature = -> Pad051
  Placement = pos=(0,0,0) rot=(1,0,0;1.5708rad)
  Radius = 3.556
FEATURE [PartDesign::Fillet] Fillet007
  Base = -> Fillet006 [Edge30,Edge31,Edge32]
  BaseFeature = -> Fillet006
  Placement = pos=(0,0,0) rot=(1,0,0;1.5708rad)
  Radius = 3.556
FEATURE [PartDesign::Body] Body042  label="1p615in_Corner_Smoothed_004"
  Group = -> [Sketch062,Pad052,Sketch061,Pad051,Fillet006,Fillet007]
  Origin = -> Origin042
  Placement = pos=(-2479.95,-0.0508,2459.18) rot=(0,0,-1;1.5708rad)
  Tip = -> Fillet007
FEATURE [Sketcher::SketchObject] Sketch063
  MapMode = 5
  Placement = pos=(0,0,0) rot=(1,0,0;1.5708rad)
  Support = -> [XZ_Plane043]
  sketch-geometry (4):
    g0: LineSegment StartX=41.021 StartY=41.021 StartZ=0 EndX=0 EndY=41.021 EndZ=0
    g1: LineSegment StartX=0 StartY=41.021 StartZ=0 EndX=0 EndY=0 EndZ=0
    g2: LineSegment StartX=0 StartY=0 StartZ=0 EndX=41.021 EndY=0 EndZ=0
    g3: LineSegment StartX=41.021 StartY=0 StartZ=0 EndX=41.021 EndY=41.021 EndZ=0
  constraints (11):
    c: Coincident(g0,g1)
    c: Coincident(g1,g2)
    c: Coincident(g2,g3)
    c: Coincident(g3,g0)
    c: Horizontal(g0)
    c: Horizontal(g2)
    c: Vertical(g1)
    c: Vertical(g3)
    c: Coincident(g1,g-1)
    c: Equal(g0,g3)
    c: DistanceX(g0,g0) = 41.021
FEATURE [PartDesign::Pad] Pad053
  Length = 41.021
  Length2 = 100
  Placement = pos=(0,0,0) rot=(1,0,0;1.5708rad)
  Profile = -> Sketch063
  Type = 0
FEATURE [Sketcher::SketchObject] Sketch064
  MapMode = 5
  Placement = pos=(0,0,0) rot=(1,0,0;3.14159rad)
  Support = -> [Pad053]
  sketch-geometry (7):
    g0: LineSegment StartX=7.5534 StartY=33.4614 StartZ=0 EndX=33.4614 EndY=33.4614 EndZ=0
    g1: LineSegment StartX=33.4614 StartY=33.4614 StartZ=0 EndX=33.4614 EndY=7.5534 EndZ=0
    g2: LineSegment StartX=33.4614 StartY=7.5534 StartZ=0 EndX=7.5534 EndY=7.5534 EndZ=0
    g3: LineSegment StartX=7.5534 StartY=7.5534 StartZ=0 EndX=7.5534 EndY=33.4614 EndZ=0
    g4: LineSegment [constr] StartX=0 StartY=0 StartZ=0 EndX=7.5534 EndY=7.5534 EndZ=0
    g5: LineSegment [constr] StartX=20.5074 StartY=20.5074 StartZ=0 EndX=7.5534 EndY=7.5534 EndZ=0
    g6: LineSegment [constr] StartX=20.5074 StartY=20.5074 StartZ=0 EndX=33.4614 EndY=33.4614 EndZ=0
  constraints (19):
    c: Coincident(g0,g1)
    c: Coincident(g1,g2)
    c: Coincident(g2,g3)
    c: Coincident(g3,g0)
    c: Horizontal(g0)
    c: Horizontal(g2)
    c: Vertical(g1)
    c: Vertical(g3)
    c: Equal(g2,g3)
    c: Coincident(g4,g-1)
    c: Coincident(g4,g2)
    c: Coincident(g5,g2)
    c: Parallel(g5,g4)
    c: Distance(g-1,g5) = 29.0018
    c: Angle(g-1,g4) = 0.785398
    c: Coincident(g6,g5)
    c: Coincident(g6,g0)
    c: Equal(g6,g5)
    c: DistanceX(g0,g0) = 25.908
FEATURE [PartDesign::Pad] Pad054
  BaseFeature = -> Pad053
  Length = 6.35
  Length2 = 100
  Placement = pos=(0,0,0) rot=(1,0,0;1.5708rad)
  Profile = -> Sketch064
  Type = 0
FEATURE [PartDesign::Fillet] Fillet009
  Base = -> Pad054 [Edge24,Edge19,Edge23,Edge21]
  BaseFeature = -> Pad054
  Placement = pos=(0,0,0) rot=(1,0,0;1.5708rad)
  Radius = 3.556
FEATURE [PartDesign::Fillet] Fillet008
  Base = -> Fillet009 [Edge30,Edge31,Edge32]
  BaseFeature = -> Fillet009
  Placement = pos=(0,0,0) rot=(1,0,0;1.5708rad)
  Radius = 3.556
FEATURE [PartDesign::Body] Body043  label="1p615in_Corner_Smoothed_005"
  Group = -> [Sketch063,Pad053,Sketch064,Pad054,Fillet009,Fillet008]
  Origin = -> Origin043
  Placement = pos=(-2479.95,2438.78,2459.18) rot=(0,0,1;3.14159rad)
  Tip = -> Fillet008
FEATURE [Sketcher::SketchObject] Sketch066
  MapMode = 5
  Placement = pos=(0,0,0) rot=(1,0,0;1.5708rad)
  Support = -> [XZ_Plane044]
  sketch-geometry (4):
    g0: LineSegment StartX=41.021 StartY=41.021 StartZ=0 EndX=0 EndY=41.021 EndZ=0
    g1: LineSegment StartX=0 StartY=41.021 StartZ=0 EndX=0 EndY=0 EndZ=0
    g2: LineSegment StartX=0 StartY=0 StartZ=0 EndX=41.021 EndY=0 EndZ=0
    g3: LineSegment StartX=41.021 StartY=0 StartZ=0 EndX=41.021 EndY=41.021 EndZ=0
  constraints (11):
    c: Coincident(g0,g1)
    c: Coincident(g1,g2)
    c: Coincident(g2,g3)
    c: Coincident(g3,g0)
    c: Horizontal(g0)
    c: Horizontal(g2)
    c: Vertical(g1)
    c: Vertical(g3)
    c: Coincident(g1,g-1)
    c: Equal(g0,g3)
    c: DistanceX(g0,g0) = 41.021
FEATURE [PartDesign::Pad] Pad055
  Length = 41.021
  Length2 = 100
  Placement = pos=(0,0,0) rot=(1,0,0;1.5708rad)
  Profile = -> Sketch066
  Type = 0
FEATURE [Sketcher::SketchObject] Sketch065
  MapMode = 5
  Placement = pos=(0,0,0) rot=(1,0,0;3.14159rad)
  Support = -> [Pad055]
  sketch-geometry (7):
    g0: LineSegment StartX=7.5534 StartY=33.4614 StartZ=0 EndX=33.4614 EndY=33.4614 EndZ=0
    g1: LineSegment StartX=33.4614 StartY=33.4614 StartZ=0 EndX=33.4614 EndY=7.5534 EndZ=0
    g2: LineSegment StartX=33.4614 StartY=7.5534 StartZ=0 EndX=7.5534 EndY=7.5534 EndZ=0
    g3: LineSegment StartX=7.5534 StartY=7.5534 StartZ=0 EndX=7.5534 EndY=33.4614 EndZ=0
    g4: LineSegment [constr] StartX=0 StartY=0 StartZ=0 EndX=7.5534 EndY=7.5534 EndZ=0
    g5: LineSegment [constr] StartX=20.5074 StartY=20.5074 StartZ=0 EndX=7.5534 EndY=7.5534 EndZ=0
    g6: LineSegment [constr] StartX=20.5074 StartY=20.5074 StartZ=0 EndX=33.4614 EndY=33.4614 EndZ=0
  constraints (19):
    c: Coincident(g0,g1)
    c: Coincident(g1,g2)
    c: Coincident(g2,g3)
    c: Coincident(g3,g0)
    c: Horizontal(g0)
    c: Horizontal(g2)
    c: Vertical(g1)
    c: Vertical(g3)
    c: Equal(g2,g3)
    c: Coincident(g4,g-1)
    c: Coincident(g4,g2)
    c: Coincident(g5,g2)
    c: Parallel(g5,g4)
    c: Distance(g-1,g5) = 29.0018
    c: Angle(g-1,g4) = 0.785398
    c: Coincident(g6,g5)
    c: Coincident(g6,g0)
    c: Equal(g6,g5)
    c: DistanceX(g0,g0) = 25.908
FEATURE [PartDesign::Pad] Pad056
  BaseFeature = -> Pad055
  Length = 6.35
  Length2 = 100
  Placement = pos=(0,0,0) rot=(1,0,0;1.5708rad)
  Profile = -> Sketch065
  Type = 0
FEATURE [PartDesign::Fillet] Fillet010
  Base = -> Pad056 [Edge24,Edge19,Edge23,Edge21]
  BaseFeature = -> Pad056
  Placement = pos=(0,0,0) rot=(1,0,0;1.5708rad)
  Radius = 3.556
FEATURE [PartDesign::Fillet] Fillet011
  Base = -> Fillet010 [Edge30,Edge31,Edge32]
  BaseFeature = -> Fillet010
  Placement = pos=(0,0,0) rot=(1,0,0;1.5708rad)
  Radius = 3.556
FEATURE [PartDesign::Body] Body044  label="1p615in_Corner_Smoothed_006"
  Group = -> [Sketch066,Pad055,Sketch065,Pad056,Fillet010,Fillet011]
  Origin = -> Origin044
  Placement = pos=(-41.1226,2438.78,2459.18) rot=(0,0,-1;4.71239rad)
  Tip = -> Fillet011
